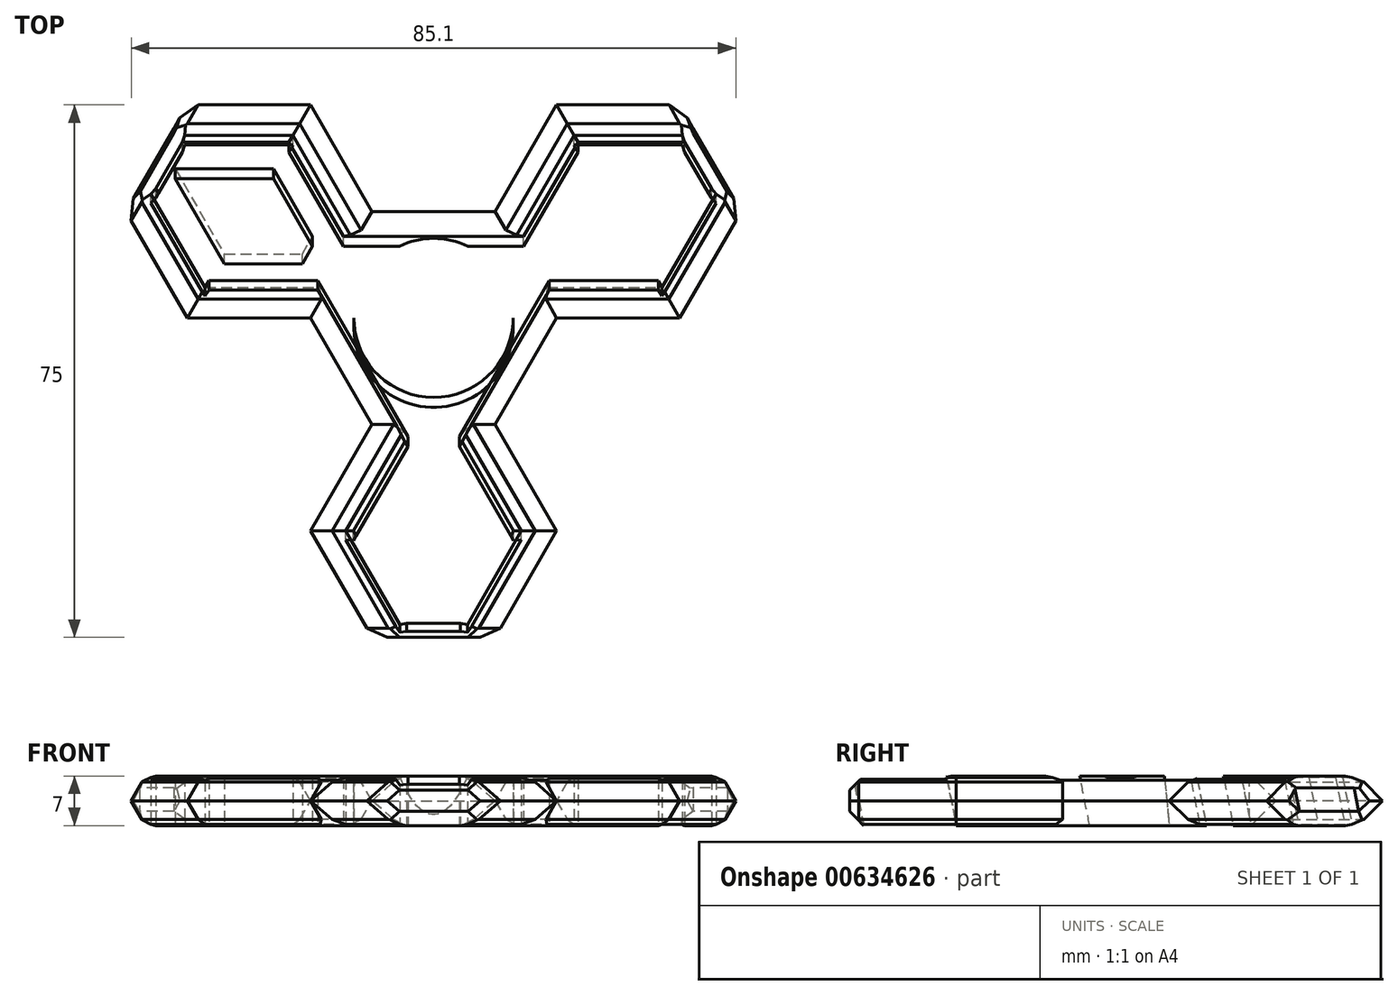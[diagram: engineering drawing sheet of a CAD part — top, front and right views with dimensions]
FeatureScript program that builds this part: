
annotation { "Feature Type Name" : "Feature", "Feature Type Description" : "" }
export const myFeature = defineFeature(function(context is Context, id is Id, definition is map)
    precondition{}
    {
        {
            var Q0;
            Q0=qCreatedBy(makeId("Top.planeOp"),FACE);
            var sketch = newSketch(context, id + "F0", { "sketchPlane" : qUnion([Q0])});
            skCircle(sketch, "E0", {"center": v(0, 0) * mm, "radius": 11.2 * mm});
            skCircle(sketch, "E1", {"center": v(0, 0) * mm, "radius": 15 * mm});
            skCircle(sketch, "E2.cCircle", {"center": v(0, 0) * mm, "radius": 15 * mm, "construction": true});
            skLineSegment(sketch, "E2.0", {"start": v(-8.66, 15) * mm, "end": v(8.66, 15) * mm});
            skLineSegment(sketch, "E2.1", {"start": v(8.66, 15) * mm, "end": v(17.32, 0) * mm});
            skLineSegment(sketch, "E2.2", {"start": v(17.32, 0) * mm, "end": v(8.66, -15) * mm});
            skLineSegment(sketch, "E2.3", {"start": v(8.66, -15) * mm, "end": v(-8.66, -15) * mm});
            skLineSegment(sketch, "E2.4", {"start": v(-8.66, -15) * mm, "end": v(-17.32, 0) * mm});
            skLineSegment(sketch, "E2.5", {"start": v(-17.32, 0) * mm, "end": v(-8.66, 15) * mm});
            skPoint(sketch, "E2.0.midPoint", {"position": v(0, 15) * mm});
            skLineSegment(sketch, "E3", {"start": v(-13, 7.5) * mm, "end": v(0, 0) * mm});
            skLineSegment(sketch, "E4", {"start": v(0, 0) * mm, "end": v(13, 7.5) * mm});
            skLineSegment(sketch, "E5", {"start": v(13, 7.5) * mm, "end": v(0, 0) * mm});
            skLineSegment(sketch, "E6", {"start": v(0, 0) * mm, "end": v(0, -15) * mm});
            skLineSegment(sketch, "E7", {"start": v(0, -15) * mm, "end": v(0, 0) * mm});
            skLineSegment(sketch, "E8", {"start": v(0, 0) * mm, "end": v(-34.64, 20) * mm});
            skLineSegment(sketch, "E9", {"start": v(-34.64, 20) * mm, "end": v(0, 0) * mm});
            skLineSegment(sketch, "E10", {"start": v(0, 0) * mm, "end": v(0, -40) * mm});
            skLineSegment(sketch, "E11", {"start": v(0, 0) * mm, "end": v(34.64, 20) * mm});
            skLineSegment(sketch, "E12", {"start": v(34.64, 20) * mm, "end": v(17.32, 10) * mm});
            skLineSegment(sketch, "E13", {"start": v(17.32, 10) * mm, "end": v(25.98, 15) * mm});
            skCircle(sketch, "E14.cCircle", {"center": v(25.98, 15) * mm, "radius": 15 * mm, "construction": true});
            skLineSegment(sketch, "E14.0", {"start": v(17.32, 0) * mm, "end": v(8.66, 15) * mm});
            skLineSegment(sketch, "E14.1", {"start": v(8.66, 15) * mm, "end": v(17.32, 30) * mm});
            skLineSegment(sketch, "E14.2", {"start": v(17.32, 30) * mm, "end": v(34.64, 30) * mm});
            skLineSegment(sketch, "E14.3", {"start": v(34.64, 30) * mm, "end": v(43.3, 15) * mm});
            skLineSegment(sketch, "E14.4", {"start": v(43.3, 15) * mm, "end": v(34.64, 0) * mm});
            skLineSegment(sketch, "E14.5", {"start": v(34.64, 0) * mm, "end": v(17.32, 0) * mm});
            skPoint(sketch, "E14.0.midPoint", {"position": v(13, 7.5) * mm});
            skCircle(sketch, "E15.cCircle", {"center": v(-25.98, 15) * mm, "radius": 15 * mm, "construction": true});
            skLineSegment(sketch, "E15.0", {"start": v(-8.66, 15) * mm, "end": v(-17.32, 0) * mm});
            skLineSegment(sketch, "E15.1", {"start": v(-17.32, 0) * mm, "end": v(-34.64, 0) * mm});
            skLineSegment(sketch, "E15.2", {"start": v(-34.64, 0) * mm, "end": v(-43.3, 15) * mm});
            skLineSegment(sketch, "E15.3", {"start": v(-43.3, 15) * mm, "end": v(-34.64, 30) * mm});
            skLineSegment(sketch, "E15.4", {"start": v(-34.64, 30) * mm, "end": v(-17.32, 30) * mm});
            skLineSegment(sketch, "E15.5", {"start": v(-17.32, 30) * mm, "end": v(-8.66, 15) * mm});
            skPoint(sketch, "E15.0.midPoint", {"position": v(-13, 7.5) * mm});
            skLineSegment(sketch, "E16", {"start": v(0, 0) * mm, "end": v(0, -20) * mm});
            skLineSegment(sketch, "E17", {"start": v(0, -20) * mm, "end": v(0, -30) * mm});
            skLineSegment(sketch, "E18", {"start": v(0, -20) * mm, "end": v(0, -40) * mm});
            skCircle(sketch, "E19.cCircle", {"center": v(0, -30) * mm, "radius": 15 * mm, "construction": true});
            skLineSegment(sketch, "E19.0", {"start": v(-8.66, -15) * mm, "end": v(8.66, -15) * mm});
            skLineSegment(sketch, "E19.1", {"start": v(8.66, -15) * mm, "end": v(17.32, -30) * mm});
            skLineSegment(sketch, "E19.2", {"start": v(17.32, -30) * mm, "end": v(8.66, -45) * mm});
            skLineSegment(sketch, "E19.3", {"start": v(8.66, -45) * mm, "end": v(-8.66, -45) * mm});
            skLineSegment(sketch, "E19.4", {"start": v(-8.66, -45) * mm, "end": v(-17.32, -30) * mm});
            skLineSegment(sketch, "E19.5", {"start": v(-17.32, -30) * mm, "end": v(-8.66, -15) * mm});
            skPoint(sketch, "E19.0.midPoint", {"position": v(0, -15) * mm});
            skSolve(sketch);
        }
        {
            var Q0;
            {var subQ0=sQuery(id+"F0.wireOp",EDGE,"E15.1");Q0=makeQuery(id+"F0.imprint","IMPRINT",FACE,{"disambiguationData":[TD([[makeQuery(id+"F0.imprint","IMPRINT",EDGE,{"derivedFrom":subQ0}),-1.0]])]});}
            var Q1;
            {var subQ0=sQuery(id+"F0.wireOp",EDGE,"E14.1");Q1=makeQuery(id+"F0.imprint","IMPRINT",FACE,{"disambiguationData":[TD([[makeQuery(id+"F0.imprint","IMPRINT",EDGE,{"derivedFrom":subQ0}),-1.0]])]});}
            var Q2;
            {var subQ0=sQuery(id+"F0.wireOp",EDGE,"E2.0");var subQ1=sQuery(id+"F0.wireOp",EDGE,"E1");var subQ2=makeQuery(id+"F0.imprint","INTERSECT",VERTEX,{"derivedFrom":[subQ1,subQ0]});Q2=makeQuery(id+"F0.imprint","IMPRINT",FACE,{"disambiguationData":[TD([[makeQuery(id+"F0.imprint","IMPRINT",EDGE,{"disambiguationData":[TD([[subQ2,1.0]])],"derivedFrom":subQ1}),-1.0]])]});}
            var Q3;
            {var subQ2=sQuery(id+"F0.wireOp",EDGE,"E9");var subQ4=sQuery(id+"F0.wireOp",EDGE,"E0");var subQ5=makeQuery(id+"F0.imprint","INTERSECT",VERTEX,{"derivedFrom":[subQ4,subQ2]});Q3=makeQuery(id+"F0.imprint","IMPRINT",FACE,{"disambiguationData":[TD([[makeQuery(id+"F0.imprint","IMPRINT",EDGE,{"disambiguationData":[TD([[subQ5,1.0]])],"derivedFrom":subQ4}),-1.0]])]});}
            var Q4;
            {var subQ0=sQuery(id+"F0.wireOp",EDGE,"E11");var subQ1=sQuery(id+"F0.wireOp",EDGE,"E0");var subQ2=makeQuery(id+"F0.imprint","INTERSECT",VERTEX,{"derivedFrom":[subQ1,subQ0]});Q4=makeQuery(id+"F0.imprint","IMPRINT",FACE,{"disambiguationData":[TD([[makeQuery(id+"F0.imprint","IMPRINT",EDGE,{"disambiguationData":[TD([[subQ2,1.0]])],"derivedFrom":subQ1}),-1.0]])]});}
            var Q5;
            {var subQ0=sQuery(id+"F0.wireOp",EDGE,"E2.2");var subQ1=sQuery(id+"F0.wireOp",EDGE,"E1");var subQ2=makeQuery(id+"F0.imprint","INTERSECT",VERTEX,{"derivedFrom":[subQ1,subQ0]});Q5=makeQuery(id+"F0.imprint","IMPRINT",FACE,{"disambiguationData":[TD([[makeQuery(id+"F0.imprint","IMPRINT",EDGE,{"disambiguationData":[TD([[subQ2,-1.0]])],"derivedFrom":subQ1}),-1.0]])]});}
            var Q6;
            {var subQ0=sQuery(id+"F0.wireOp",EDGE,"E19.1");Q6=makeQuery(id+"F0.imprint","IMPRINT",FACE,{"disambiguationData":[TD([[makeQuery(id+"F0.imprint","IMPRINT",EDGE,{"derivedFrom":subQ0}),-1.0]])]});}
            var Q7;
            {var subQ0=sQuery(id+"F0.wireOp",EDGE,"E2.2");var subQ1=sQuery(id+"F0.wireOp",EDGE,"E1");var subQ2=makeQuery(id+"F0.imprint","INTERSECT",VERTEX,{"derivedFrom":[subQ1,subQ0]});Q7=makeQuery(id+"F0.imprint","IMPRINT",FACE,{"disambiguationData":[TD([[makeQuery(id+"F0.imprint","IMPRINT",EDGE,{"disambiguationData":[TD([[subQ2,1.0]])],"derivedFrom":subQ1}),-1.0]])]});}
            var Q8;
            {var subQ0=sQuery(id+"F0.wireOp",EDGE,"E2.4");var subQ1=sQuery(id+"F0.wireOp",EDGE,"E1");var subQ2=makeQuery(id+"F0.imprint","INTERSECT",VERTEX,{"derivedFrom":[subQ1,subQ0]});Q8=makeQuery(id+"F0.imprint","IMPRINT",FACE,{"disambiguationData":[TD([[makeQuery(id+"F0.imprint","IMPRINT",EDGE,{"disambiguationData":[TD([[subQ2,-1.0]])],"derivedFrom":subQ1}),-1.0]])]});}
            var Q9;
            {var subQ0=sQuery(id+"F0.wireOp",EDGE,"E9");var subQ1=sQuery(id+"F0.wireOp",EDGE,"E0");var subQ2=makeQuery(id+"F0.imprint","INTERSECT",VERTEX,{"derivedFrom":[subQ1,subQ0]});Q9=makeQuery(id+"F0.imprint","IMPRINT",FACE,{"disambiguationData":[TD([[makeQuery(id+"F0.imprint","IMPRINT",EDGE,{"disambiguationData":[TD([[subQ2,-1.0]])],"derivedFrom":subQ1}),-1.0]])]});}
            var Q10;
            {var subQ0=sQuery(id+"F0.wireOp",EDGE,"E2.4");var subQ1=sQuery(id+"F0.wireOp",EDGE,"E1");var subQ2=makeQuery(id+"F0.imprint","INTERSECT",VERTEX,{"derivedFrom":[subQ1,subQ0]});Q10=makeQuery(id+"F0.imprint","IMPRINT",FACE,{"disambiguationData":[TD([[makeQuery(id+"F0.imprint","IMPRINT",EDGE,{"disambiguationData":[TD([[subQ2,1.0]])],"derivedFrom":subQ1}),-1.0]])]});}
            var Q11;
            {var subQ0=sQuery(id+"F0.wireOp",EDGE,"E2.0");var subQ1=sQuery(id+"F0.wireOp",EDGE,"E1");var subQ2=makeQuery(id+"F0.imprint","INTERSECT",VERTEX,{"derivedFrom":[subQ1,subQ0]});Q11=makeQuery(id+"F0.imprint","IMPRINT",FACE,{"disambiguationData":[TD([[makeQuery(id+"F0.imprint","IMPRINT",EDGE,{"disambiguationData":[TD([[subQ2,-1.0]])],"derivedFrom":subQ1}),-1.0]])]});}
            extrude(context, id + "F1", {"entities" : qUnion([Q0, Q1, Q2, Q3, Q4, Q5, Q6, Q7, Q8, Q9, Q10, Q11]), "depth" : 7 * mm, "offsetDistance" : 25 * mm});
        }
        {
            var Q0;
            Q0=makeQuery(id+"F1.opExtrude","CAP_EDGE",EDGE,{"disambiguationData":[OSD([sQuery(id+"F0.wireOp",EDGE,"E14.2")])],"isStart":true});
            var Q1;
            Q1=makeQuery(id+"F1.opExtrude","CAP_EDGE",EDGE,{"disambiguationData":[OSD([sQuery(id+"F0.wireOp",EDGE,"E14.1")])],"isStart":true});
            var Q2;
            Q2=makeQuery(id+"F1.opExtrude","CAP_EDGE",EDGE,{"disambiguationData":[OSD([sQuery(id+"F0.wireOp",EDGE,"E2.0")])],"isStart":true});
            var Q3;
            Q3=makeQuery(id+"F1.opExtrude","CAP_EDGE",EDGE,{"disambiguationData":[OSD([sQuery(id+"F0.wireOp",EDGE,"E15.5")])],"isStart":true});
            var Q4;
            Q4=makeQuery(id+"F1.opExtrude","CAP_EDGE",EDGE,{"disambiguationData":[OSD([sQuery(id+"F0.wireOp",EDGE,"E15.4")])],"isStart":true});
            var Q5;
            Q5=makeQuery(id+"F1.opExtrude","CAP_EDGE",EDGE,{"disambiguationData":[OSD([sQuery(id+"F0.wireOp",EDGE,"E15.2")])],"isStart":true});
            var Q6;
            Q6=makeQuery(id+"F1.opExtrude","CAP_EDGE",EDGE,{"disambiguationData":[OSD([sQuery(id+"F0.wireOp",EDGE,"E15.1")])],"isStart":true});
            var Q7;
            Q7=makeQuery(id+"F1.opExtrude","CAP_EDGE",EDGE,{"disambiguationData":[OSD([sQuery(id+"F0.wireOp",EDGE,"E2.4")])],"isStart":true});
            var Q8;
            Q8=makeQuery(id+"F1.opExtrude","CAP_EDGE",EDGE,{"disambiguationData":[OSD([sQuery(id+"F0.wireOp",EDGE,"E19.5")])],"isStart":true});
            var Q9;
            Q9=makeQuery(id+"F1.opExtrude","CAP_EDGE",EDGE,{"disambiguationData":[OSD([sQuery(id+"F0.wireOp",EDGE,"E19.4")])],"isStart":true});
            var Q10;
            Q10=makeQuery(id+"F1.opExtrude","CAP_EDGE",EDGE,{"disambiguationData":[OSD([sQuery(id+"F0.wireOp",EDGE,"E19.2")])],"isStart":true});
            var Q11;
            Q11=makeQuery(id+"F1.opExtrude","CAP_EDGE",EDGE,{"disambiguationData":[OSD([sQuery(id+"F0.wireOp",EDGE,"E19.1")])],"isStart":true});
            var Q12;
            Q12=makeQuery(id+"F1.opExtrude","CAP_EDGE",EDGE,{"disambiguationData":[OSD([sQuery(id+"F0.wireOp",EDGE,"E2.2")])],"isStart":true});
            var Q13;
            Q13=makeQuery(id+"F1.opExtrude","CAP_EDGE",EDGE,{"disambiguationData":[OSD([sQuery(id+"F0.wireOp",EDGE,"E14.5")])],"isStart":true});
            var Q14;
            Q14=makeQuery(id+"F1.opExtrude","CAP_EDGE",EDGE,{"disambiguationData":[OSD([sQuery(id+"F0.wireOp",EDGE,"E14.4")])],"isStart":true});
            var Q15;
            Q15=makeQuery(id+"F1.opExtrude","CAP_EDGE",EDGE,{"disambiguationData":[OSD([sQuery(id+"F0.wireOp",EDGE,"E15.4")])],"isStart":false});
            var Q16;
            Q16=makeQuery(id+"F1.opExtrude","CAP_EDGE",EDGE,{"disambiguationData":[OSD([sQuery(id+"F0.wireOp",EDGE,"E15.5")])],"isStart":false});
            var Q17;
            Q17=makeQuery(id+"F1.opExtrude","CAP_EDGE",EDGE,{"disambiguationData":[OSD([sQuery(id+"F0.wireOp",EDGE,"E2.0")])],"isStart":false});
            var Q18;
            Q18=makeQuery(id+"F1.opExtrude","CAP_EDGE",EDGE,{"disambiguationData":[OSD([sQuery(id+"F0.wireOp",EDGE,"E14.1")])],"isStart":false});
            var Q19;
            Q19=makeQuery(id+"F1.opExtrude","CAP_EDGE",EDGE,{"disambiguationData":[OSD([sQuery(id+"F0.wireOp",EDGE,"E14.2")])],"isStart":false});
            var Q20;
            Q20=makeQuery(id+"F1.opExtrude","CAP_EDGE",EDGE,{"disambiguationData":[OSD([sQuery(id+"F0.wireOp",EDGE,"E14.4")])],"isStart":false});
            var Q21;
            Q21=makeQuery(id+"F1.opExtrude","CAP_EDGE",EDGE,{"disambiguationData":[OSD([sQuery(id+"F0.wireOp",EDGE,"E2.2")])],"isStart":false});
            var Q22;
            Q22=makeQuery(id+"F1.opExtrude","CAP_EDGE",EDGE,{"disambiguationData":[OSD([sQuery(id+"F0.wireOp",EDGE,"E14.5")])],"isStart":false});
            var Q23;
            Q23=makeQuery(id+"F1.opExtrude","CAP_EDGE",EDGE,{"disambiguationData":[OSD([sQuery(id+"F0.wireOp",EDGE,"E19.1")])],"isStart":false});
            var Q24;
            Q24=makeQuery(id+"F1.opExtrude","CAP_EDGE",EDGE,{"disambiguationData":[OSD([sQuery(id+"F0.wireOp",EDGE,"E19.2")])],"isStart":false});
            var Q25;
            Q25=makeQuery(id+"F1.opExtrude","CAP_EDGE",EDGE,{"disambiguationData":[OSD([sQuery(id+"F0.wireOp",EDGE,"E19.4")])],"isStart":false});
            var Q26;
            Q26=makeQuery(id+"F1.opExtrude","CAP_EDGE",EDGE,{"disambiguationData":[OSD([sQuery(id+"F0.wireOp",EDGE,"E19.5")])],"isStart":false});
            var Q27;
            Q27=makeQuery(id+"F1.opExtrude","CAP_EDGE",EDGE,{"disambiguationData":[OSD([sQuery(id+"F0.wireOp",EDGE,"E2.4")])],"isStart":false});
            var Q28;
            Q28=makeQuery(id+"F1.opExtrude","CAP_EDGE",EDGE,{"disambiguationData":[OSD([sQuery(id+"F0.wireOp",EDGE,"E15.2")])],"isStart":false});
            chamfer(context, id + "F2", {"entities" : qUnion([Q0, Q1, Q2, Q3, Q4, Q5, Q6, Q7, Q8, Q9, Q10, Q11, Q12, Q13, Q14, Q15, Q16, Q17, Q18, Q19, Q20, Q21, Q22, Q23, Q24, Q25, Q26, Q27, Q28]), "width" : 3.5 * mm, "tangentPropagation" : true});
        }
        {
            var Q0;
            Q0=makeQuery(id+"F1.opExtrude","CAP_EDGE",EDGE,{"disambiguationData":[OSD([sQuery(id+"F0.wireOp",EDGE,"E15.1")])],"isStart":false});
            chamfer(context, id + "F3", {"entities" : qUnion([Q0]), "width" : 3.5 * mm, "tangentPropagation" : true});
        }
        {
            var Q0;
            Q0=makeQuery(id+"F1.opExtrude","SWEPT_FACE",FACE,{"disambiguationData":[OSD([sQuery(id+"F0.wireOp",EDGE,"E14.3")])]});
            var Q1;
            Q1=makeQuery(id+"F1.opExtrude","SWEPT_FACE",FACE,{"disambiguationData":[OSD([sQuery(id+"F0.wireOp",EDGE,"E15.3")])]});
            var Q2;
            Q2=makeQuery(id+"F1.opExtrude","SWEPT_FACE",FACE,{"disambiguationData":[OSD([sQuery(id+"F0.wireOp",EDGE,"E19.3")])]});
            chamfer(context, id + "F4", {"entities" : qUnion([Q0, Q1, Q2]), "width" : 2 * mm, "tangentPropagation" : true});
        }
        {
            var Q0;
            {var subQ0=sQuery(id+"F0.wireOp",EDGE,"E19.5");Q0=makeQuery(id+"F2.opChamfer","BLEND_EDGE",EDGE,{"blendedFrom":[makeQuery(id+"F1.opExtrude","CAP_EDGE",EDGE,{"disambiguationData":[OSD([subQ0])],"isStart":false}),makeQuery(id+"F1.opExtrude","CAP_FACE",FACE,{"disambiguationData":[OSD([sQuery(id+"F0.wireOp",EDGE,"E0"),sQuery(id+"F0.wireOp",EDGE,"E2.0"),sQuery(id+"F0.wireOp",EDGE,"E2.2"),sQuery(id+"F0.wireOp",EDGE,"E2.4"),sQuery(id+"F0.wireOp",EDGE,"E14.1"),sQuery(id+"F0.wireOp",EDGE,"E14.2"),sQuery(id+"F0.wireOp",EDGE,"E14.3"),sQuery(id+"F0.wireOp",EDGE,"E14.4"),sQuery(id+"F0.wireOp",EDGE,"E14.5"),sQuery(id+"F0.wireOp",EDGE,"E15.1"),sQuery(id+"F0.wireOp",EDGE,"E15.2"),sQuery(id+"F0.wireOp",EDGE,"E15.3"),sQuery(id+"F0.wireOp",EDGE,"E15.4"),sQuery(id+"F0.wireOp",EDGE,"E15.5"),sQuery(id+"F0.wireOp",EDGE,"E19.1"),sQuery(id+"F0.wireOp",EDGE,"E19.2"),sQuery(id+"F0.wireOp",EDGE,"E19.3"),sQuery(id+"F0.wireOp",EDGE,"E19.4"),subQ0])],"isStart":false})],"blendedInto":[makeQuery(id+"F1.opExtrude","CAP_FACE",FACE,{"disambiguationData":[OSD([sQuery(id+"F0.wireOp",EDGE,"E0"),sQuery(id+"F0.wireOp",EDGE,"E2.0"),sQuery(id+"F0.wireOp",EDGE,"E2.2"),sQuery(id+"F0.wireOp",EDGE,"E2.4"),sQuery(id+"F0.wireOp",EDGE,"E14.1"),sQuery(id+"F0.wireOp",EDGE,"E14.2"),sQuery(id+"F0.wireOp",EDGE,"E14.3"),sQuery(id+"F0.wireOp",EDGE,"E14.4"),sQuery(id+"F0.wireOp",EDGE,"E14.5"),sQuery(id+"F0.wireOp",EDGE,"E15.1"),sQuery(id+"F0.wireOp",EDGE,"E15.2"),sQuery(id+"F0.wireOp",EDGE,"E15.3"),sQuery(id+"F0.wireOp",EDGE,"E15.4"),sQuery(id+"F0.wireOp",EDGE,"E15.5"),sQuery(id+"F0.wireOp",EDGE,"E19.1"),sQuery(id+"F0.wireOp",EDGE,"E19.2"),sQuery(id+"F0.wireOp",EDGE,"E19.3"),sQuery(id+"F0.wireOp",EDGE,"E19.4"),subQ0])],"isStart":false})]});}
            var Q1;
            {var subQ0=sQuery(id+"F0.wireOp",EDGE,"E19.4");Q1=makeQuery(id+"F2.opChamfer","BLEND_EDGE",EDGE,{"blendedFrom":[makeQuery(id+"F1.opExtrude","CAP_EDGE",EDGE,{"disambiguationData":[OSD([subQ0])],"isStart":false}),makeQuery(id+"F1.opExtrude","CAP_FACE",FACE,{"disambiguationData":[OSD([sQuery(id+"F0.wireOp",EDGE,"E0"),sQuery(id+"F0.wireOp",EDGE,"E2.0"),sQuery(id+"F0.wireOp",EDGE,"E2.2"),sQuery(id+"F0.wireOp",EDGE,"E2.4"),sQuery(id+"F0.wireOp",EDGE,"E14.1"),sQuery(id+"F0.wireOp",EDGE,"E14.2"),sQuery(id+"F0.wireOp",EDGE,"E14.3"),sQuery(id+"F0.wireOp",EDGE,"E14.4"),sQuery(id+"F0.wireOp",EDGE,"E14.5"),sQuery(id+"F0.wireOp",EDGE,"E15.1"),sQuery(id+"F0.wireOp",EDGE,"E15.2"),sQuery(id+"F0.wireOp",EDGE,"E15.3"),sQuery(id+"F0.wireOp",EDGE,"E15.4"),sQuery(id+"F0.wireOp",EDGE,"E15.5"),sQuery(id+"F0.wireOp",EDGE,"E19.1"),sQuery(id+"F0.wireOp",EDGE,"E19.2"),sQuery(id+"F0.wireOp",EDGE,"E19.3"),subQ0,sQuery(id+"F0.wireOp",EDGE,"E19.5")])],"isStart":false})],"blendedInto":[makeQuery(id+"F1.opExtrude","CAP_FACE",FACE,{"disambiguationData":[OSD([sQuery(id+"F0.wireOp",EDGE,"E0"),sQuery(id+"F0.wireOp",EDGE,"E2.0"),sQuery(id+"F0.wireOp",EDGE,"E2.2"),sQuery(id+"F0.wireOp",EDGE,"E2.4"),sQuery(id+"F0.wireOp",EDGE,"E14.1"),sQuery(id+"F0.wireOp",EDGE,"E14.2"),sQuery(id+"F0.wireOp",EDGE,"E14.3"),sQuery(id+"F0.wireOp",EDGE,"E14.4"),sQuery(id+"F0.wireOp",EDGE,"E14.5"),sQuery(id+"F0.wireOp",EDGE,"E15.1"),sQuery(id+"F0.wireOp",EDGE,"E15.2"),sQuery(id+"F0.wireOp",EDGE,"E15.3"),sQuery(id+"F0.wireOp",EDGE,"E15.4"),sQuery(id+"F0.wireOp",EDGE,"E15.5"),sQuery(id+"F0.wireOp",EDGE,"E19.1"),sQuery(id+"F0.wireOp",EDGE,"E19.2"),sQuery(id+"F0.wireOp",EDGE,"E19.3"),subQ0,sQuery(id+"F0.wireOp",EDGE,"E19.5")])],"isStart":false})]});}
            var Q2;
            {var subQ0=sQuery(id+"F0.wireOp",EDGE,"E19.2");Q2=makeQuery(id+"F2.opChamfer","BLEND_EDGE",EDGE,{"blendedFrom":[makeQuery(id+"F1.opExtrude","CAP_EDGE",EDGE,{"disambiguationData":[OSD([subQ0])],"isStart":false}),makeQuery(id+"F1.opExtrude","CAP_FACE",FACE,{"disambiguationData":[OSD([sQuery(id+"F0.wireOp",EDGE,"E0"),sQuery(id+"F0.wireOp",EDGE,"E2.0"),sQuery(id+"F0.wireOp",EDGE,"E2.2"),sQuery(id+"F0.wireOp",EDGE,"E2.4"),sQuery(id+"F0.wireOp",EDGE,"E14.1"),sQuery(id+"F0.wireOp",EDGE,"E14.2"),sQuery(id+"F0.wireOp",EDGE,"E14.3"),sQuery(id+"F0.wireOp",EDGE,"E14.4"),sQuery(id+"F0.wireOp",EDGE,"E14.5"),sQuery(id+"F0.wireOp",EDGE,"E15.1"),sQuery(id+"F0.wireOp",EDGE,"E15.2"),sQuery(id+"F0.wireOp",EDGE,"E15.3"),sQuery(id+"F0.wireOp",EDGE,"E15.4"),sQuery(id+"F0.wireOp",EDGE,"E15.5"),sQuery(id+"F0.wireOp",EDGE,"E19.1"),subQ0,sQuery(id+"F0.wireOp",EDGE,"E19.3"),sQuery(id+"F0.wireOp",EDGE,"E19.4"),sQuery(id+"F0.wireOp",EDGE,"E19.5")])],"isStart":false})],"blendedInto":[makeQuery(id+"F1.opExtrude","CAP_FACE",FACE,{"disambiguationData":[OSD([sQuery(id+"F0.wireOp",EDGE,"E0"),sQuery(id+"F0.wireOp",EDGE,"E2.0"),sQuery(id+"F0.wireOp",EDGE,"E2.2"),sQuery(id+"F0.wireOp",EDGE,"E2.4"),sQuery(id+"F0.wireOp",EDGE,"E14.1"),sQuery(id+"F0.wireOp",EDGE,"E14.2"),sQuery(id+"F0.wireOp",EDGE,"E14.3"),sQuery(id+"F0.wireOp",EDGE,"E14.4"),sQuery(id+"F0.wireOp",EDGE,"E14.5"),sQuery(id+"F0.wireOp",EDGE,"E15.1"),sQuery(id+"F0.wireOp",EDGE,"E15.2"),sQuery(id+"F0.wireOp",EDGE,"E15.3"),sQuery(id+"F0.wireOp",EDGE,"E15.4"),sQuery(id+"F0.wireOp",EDGE,"E15.5"),sQuery(id+"F0.wireOp",EDGE,"E19.1"),subQ0,sQuery(id+"F0.wireOp",EDGE,"E19.3"),sQuery(id+"F0.wireOp",EDGE,"E19.4"),sQuery(id+"F0.wireOp",EDGE,"E19.5")])],"isStart":false})]});}
            var Q3;
            {var subQ0=sQuery(id+"F0.wireOp",EDGE,"E19.1");Q3=makeQuery(id+"F2.opChamfer","BLEND_EDGE",EDGE,{"blendedFrom":[makeQuery(id+"F1.opExtrude","CAP_EDGE",EDGE,{"disambiguationData":[OSD([subQ0])],"isStart":false}),makeQuery(id+"F1.opExtrude","CAP_FACE",FACE,{"disambiguationData":[OSD([sQuery(id+"F0.wireOp",EDGE,"E0"),sQuery(id+"F0.wireOp",EDGE,"E2.0"),sQuery(id+"F0.wireOp",EDGE,"E2.2"),sQuery(id+"F0.wireOp",EDGE,"E2.4"),sQuery(id+"F0.wireOp",EDGE,"E14.1"),sQuery(id+"F0.wireOp",EDGE,"E14.2"),sQuery(id+"F0.wireOp",EDGE,"E14.3"),sQuery(id+"F0.wireOp",EDGE,"E14.4"),sQuery(id+"F0.wireOp",EDGE,"E14.5"),sQuery(id+"F0.wireOp",EDGE,"E15.1"),sQuery(id+"F0.wireOp",EDGE,"E15.2"),sQuery(id+"F0.wireOp",EDGE,"E15.3"),sQuery(id+"F0.wireOp",EDGE,"E15.4"),sQuery(id+"F0.wireOp",EDGE,"E15.5"),subQ0,sQuery(id+"F0.wireOp",EDGE,"E19.2"),sQuery(id+"F0.wireOp",EDGE,"E19.3"),sQuery(id+"F0.wireOp",EDGE,"E19.4"),sQuery(id+"F0.wireOp",EDGE,"E19.5")])],"isStart":false})],"blendedInto":[makeQuery(id+"F1.opExtrude","CAP_FACE",FACE,{"disambiguationData":[OSD([sQuery(id+"F0.wireOp",EDGE,"E0"),sQuery(id+"F0.wireOp",EDGE,"E2.0"),sQuery(id+"F0.wireOp",EDGE,"E2.2"),sQuery(id+"F0.wireOp",EDGE,"E2.4"),sQuery(id+"F0.wireOp",EDGE,"E14.1"),sQuery(id+"F0.wireOp",EDGE,"E14.2"),sQuery(id+"F0.wireOp",EDGE,"E14.3"),sQuery(id+"F0.wireOp",EDGE,"E14.4"),sQuery(id+"F0.wireOp",EDGE,"E14.5"),sQuery(id+"F0.wireOp",EDGE,"E15.1"),sQuery(id+"F0.wireOp",EDGE,"E15.2"),sQuery(id+"F0.wireOp",EDGE,"E15.3"),sQuery(id+"F0.wireOp",EDGE,"E15.4"),sQuery(id+"F0.wireOp",EDGE,"E15.5"),subQ0,sQuery(id+"F0.wireOp",EDGE,"E19.2"),sQuery(id+"F0.wireOp",EDGE,"E19.3"),sQuery(id+"F0.wireOp",EDGE,"E19.4"),sQuery(id+"F0.wireOp",EDGE,"E19.5")])],"isStart":false})]});}
            var Q4;
            {var subQ0=sQuery(id+"F0.wireOp",EDGE,"E15.1");Q4=makeQuery(id+"F3.opChamfer","BLEND_EDGE",EDGE,{"blendedFrom":[makeQuery(id+"F1.opExtrude","CAP_EDGE",EDGE,{"disambiguationData":[OSD([subQ0])],"isStart":false}),makeQuery(id+"F1.opExtrude","CAP_FACE",FACE,{"disambiguationData":[OSD([sQuery(id+"F0.wireOp",EDGE,"E0"),sQuery(id+"F0.wireOp",EDGE,"E2.0"),sQuery(id+"F0.wireOp",EDGE,"E2.2"),sQuery(id+"F0.wireOp",EDGE,"E2.4"),sQuery(id+"F0.wireOp",EDGE,"E14.1"),sQuery(id+"F0.wireOp",EDGE,"E14.2"),sQuery(id+"F0.wireOp",EDGE,"E14.3"),sQuery(id+"F0.wireOp",EDGE,"E14.4"),sQuery(id+"F0.wireOp",EDGE,"E14.5"),subQ0,sQuery(id+"F0.wireOp",EDGE,"E15.2"),sQuery(id+"F0.wireOp",EDGE,"E15.3"),sQuery(id+"F0.wireOp",EDGE,"E15.4"),sQuery(id+"F0.wireOp",EDGE,"E15.5"),sQuery(id+"F0.wireOp",EDGE,"E19.1"),sQuery(id+"F0.wireOp",EDGE,"E19.2"),sQuery(id+"F0.wireOp",EDGE,"E19.3"),sQuery(id+"F0.wireOp",EDGE,"E19.4"),sQuery(id+"F0.wireOp",EDGE,"E19.5")])],"isStart":false})],"blendedInto":[makeQuery(id+"F1.opExtrude","CAP_FACE",FACE,{"disambiguationData":[OSD([sQuery(id+"F0.wireOp",EDGE,"E0"),sQuery(id+"F0.wireOp",EDGE,"E2.0"),sQuery(id+"F0.wireOp",EDGE,"E2.2"),sQuery(id+"F0.wireOp",EDGE,"E2.4"),sQuery(id+"F0.wireOp",EDGE,"E14.1"),sQuery(id+"F0.wireOp",EDGE,"E14.2"),sQuery(id+"F0.wireOp",EDGE,"E14.3"),sQuery(id+"F0.wireOp",EDGE,"E14.4"),sQuery(id+"F0.wireOp",EDGE,"E14.5"),subQ0,sQuery(id+"F0.wireOp",EDGE,"E15.2"),sQuery(id+"F0.wireOp",EDGE,"E15.3"),sQuery(id+"F0.wireOp",EDGE,"E15.4"),sQuery(id+"F0.wireOp",EDGE,"E15.5"),sQuery(id+"F0.wireOp",EDGE,"E19.1"),sQuery(id+"F0.wireOp",EDGE,"E19.2"),sQuery(id+"F0.wireOp",EDGE,"E19.3"),sQuery(id+"F0.wireOp",EDGE,"E19.4"),sQuery(id+"F0.wireOp",EDGE,"E19.5")])],"isStart":false})]});}
            var Q5;
            {var subQ0=sQuery(id+"F0.wireOp",EDGE,"E15.2");Q5=makeQuery(id+"F2.opChamfer","BLEND_EDGE",EDGE,{"blendedFrom":[makeQuery(id+"F1.opExtrude","CAP_EDGE",EDGE,{"disambiguationData":[OSD([subQ0])],"isStart":false}),makeQuery(id+"F1.opExtrude","CAP_FACE",FACE,{"disambiguationData":[OSD([sQuery(id+"F0.wireOp",EDGE,"E0"),sQuery(id+"F0.wireOp",EDGE,"E2.0"),sQuery(id+"F0.wireOp",EDGE,"E2.2"),sQuery(id+"F0.wireOp",EDGE,"E2.4"),sQuery(id+"F0.wireOp",EDGE,"E14.1"),sQuery(id+"F0.wireOp",EDGE,"E14.2"),sQuery(id+"F0.wireOp",EDGE,"E14.3"),sQuery(id+"F0.wireOp",EDGE,"E14.4"),sQuery(id+"F0.wireOp",EDGE,"E14.5"),sQuery(id+"F0.wireOp",EDGE,"E15.1"),subQ0,sQuery(id+"F0.wireOp",EDGE,"E15.3"),sQuery(id+"F0.wireOp",EDGE,"E15.4"),sQuery(id+"F0.wireOp",EDGE,"E15.5"),sQuery(id+"F0.wireOp",EDGE,"E19.1"),sQuery(id+"F0.wireOp",EDGE,"E19.2"),sQuery(id+"F0.wireOp",EDGE,"E19.3"),sQuery(id+"F0.wireOp",EDGE,"E19.4"),sQuery(id+"F0.wireOp",EDGE,"E19.5")])],"isStart":false})],"blendedInto":[makeQuery(id+"F1.opExtrude","CAP_FACE",FACE,{"disambiguationData":[OSD([sQuery(id+"F0.wireOp",EDGE,"E0"),sQuery(id+"F0.wireOp",EDGE,"E2.0"),sQuery(id+"F0.wireOp",EDGE,"E2.2"),sQuery(id+"F0.wireOp",EDGE,"E2.4"),sQuery(id+"F0.wireOp",EDGE,"E14.1"),sQuery(id+"F0.wireOp",EDGE,"E14.2"),sQuery(id+"F0.wireOp",EDGE,"E14.3"),sQuery(id+"F0.wireOp",EDGE,"E14.4"),sQuery(id+"F0.wireOp",EDGE,"E14.5"),sQuery(id+"F0.wireOp",EDGE,"E15.1"),subQ0,sQuery(id+"F0.wireOp",EDGE,"E15.3"),sQuery(id+"F0.wireOp",EDGE,"E15.4"),sQuery(id+"F0.wireOp",EDGE,"E15.5"),sQuery(id+"F0.wireOp",EDGE,"E19.1"),sQuery(id+"F0.wireOp",EDGE,"E19.2"),sQuery(id+"F0.wireOp",EDGE,"E19.3"),sQuery(id+"F0.wireOp",EDGE,"E19.4"),sQuery(id+"F0.wireOp",EDGE,"E19.5")])],"isStart":false})]});}
            var Q6;
            {var subQ0=sQuery(id+"F0.wireOp",EDGE,"E15.4");Q6=makeQuery(id+"F2.opChamfer","BLEND_EDGE",EDGE,{"blendedFrom":[makeQuery(id+"F1.opExtrude","CAP_EDGE",EDGE,{"disambiguationData":[OSD([subQ0])],"isStart":false}),makeQuery(id+"F1.opExtrude","CAP_FACE",FACE,{"disambiguationData":[OSD([sQuery(id+"F0.wireOp",EDGE,"E0"),sQuery(id+"F0.wireOp",EDGE,"E2.0"),sQuery(id+"F0.wireOp",EDGE,"E2.2"),sQuery(id+"F0.wireOp",EDGE,"E2.4"),sQuery(id+"F0.wireOp",EDGE,"E14.1"),sQuery(id+"F0.wireOp",EDGE,"E14.2"),sQuery(id+"F0.wireOp",EDGE,"E14.3"),sQuery(id+"F0.wireOp",EDGE,"E14.4"),sQuery(id+"F0.wireOp",EDGE,"E14.5"),sQuery(id+"F0.wireOp",EDGE,"E15.1"),sQuery(id+"F0.wireOp",EDGE,"E15.2"),sQuery(id+"F0.wireOp",EDGE,"E15.3"),subQ0,sQuery(id+"F0.wireOp",EDGE,"E15.5"),sQuery(id+"F0.wireOp",EDGE,"E19.1"),sQuery(id+"F0.wireOp",EDGE,"E19.2"),sQuery(id+"F0.wireOp",EDGE,"E19.3"),sQuery(id+"F0.wireOp",EDGE,"E19.4"),sQuery(id+"F0.wireOp",EDGE,"E19.5")])],"isStart":false})],"blendedInto":[makeQuery(id+"F1.opExtrude","CAP_FACE",FACE,{"disambiguationData":[OSD([sQuery(id+"F0.wireOp",EDGE,"E0"),sQuery(id+"F0.wireOp",EDGE,"E2.0"),sQuery(id+"F0.wireOp",EDGE,"E2.2"),sQuery(id+"F0.wireOp",EDGE,"E2.4"),sQuery(id+"F0.wireOp",EDGE,"E14.1"),sQuery(id+"F0.wireOp",EDGE,"E14.2"),sQuery(id+"F0.wireOp",EDGE,"E14.3"),sQuery(id+"F0.wireOp",EDGE,"E14.4"),sQuery(id+"F0.wireOp",EDGE,"E14.5"),sQuery(id+"F0.wireOp",EDGE,"E15.1"),sQuery(id+"F0.wireOp",EDGE,"E15.2"),sQuery(id+"F0.wireOp",EDGE,"E15.3"),subQ0,sQuery(id+"F0.wireOp",EDGE,"E15.5"),sQuery(id+"F0.wireOp",EDGE,"E19.1"),sQuery(id+"F0.wireOp",EDGE,"E19.2"),sQuery(id+"F0.wireOp",EDGE,"E19.3"),sQuery(id+"F0.wireOp",EDGE,"E19.4"),sQuery(id+"F0.wireOp",EDGE,"E19.5")])],"isStart":false})]});}
            var Q7;
            {var subQ0=sQuery(id+"F0.wireOp",EDGE,"E15.5");Q7=makeQuery(id+"F2.opChamfer","BLEND_EDGE",EDGE,{"blendedFrom":[makeQuery(id+"F1.opExtrude","CAP_EDGE",EDGE,{"disambiguationData":[OSD([subQ0])],"isStart":false}),makeQuery(id+"F1.opExtrude","CAP_FACE",FACE,{"disambiguationData":[OSD([sQuery(id+"F0.wireOp",EDGE,"E0"),sQuery(id+"F0.wireOp",EDGE,"E2.0"),sQuery(id+"F0.wireOp",EDGE,"E2.2"),sQuery(id+"F0.wireOp",EDGE,"E2.4"),sQuery(id+"F0.wireOp",EDGE,"E14.1"),sQuery(id+"F0.wireOp",EDGE,"E14.2"),sQuery(id+"F0.wireOp",EDGE,"E14.3"),sQuery(id+"F0.wireOp",EDGE,"E14.4"),sQuery(id+"F0.wireOp",EDGE,"E14.5"),sQuery(id+"F0.wireOp",EDGE,"E15.1"),sQuery(id+"F0.wireOp",EDGE,"E15.2"),sQuery(id+"F0.wireOp",EDGE,"E15.3"),sQuery(id+"F0.wireOp",EDGE,"E15.4"),subQ0,sQuery(id+"F0.wireOp",EDGE,"E19.1"),sQuery(id+"F0.wireOp",EDGE,"E19.2"),sQuery(id+"F0.wireOp",EDGE,"E19.3"),sQuery(id+"F0.wireOp",EDGE,"E19.4"),sQuery(id+"F0.wireOp",EDGE,"E19.5")])],"isStart":false})],"blendedInto":[makeQuery(id+"F1.opExtrude","CAP_FACE",FACE,{"disambiguationData":[OSD([sQuery(id+"F0.wireOp",EDGE,"E0"),sQuery(id+"F0.wireOp",EDGE,"E2.0"),sQuery(id+"F0.wireOp",EDGE,"E2.2"),sQuery(id+"F0.wireOp",EDGE,"E2.4"),sQuery(id+"F0.wireOp",EDGE,"E14.1"),sQuery(id+"F0.wireOp",EDGE,"E14.2"),sQuery(id+"F0.wireOp",EDGE,"E14.3"),sQuery(id+"F0.wireOp",EDGE,"E14.4"),sQuery(id+"F0.wireOp",EDGE,"E14.5"),sQuery(id+"F0.wireOp",EDGE,"E15.1"),sQuery(id+"F0.wireOp",EDGE,"E15.2"),sQuery(id+"F0.wireOp",EDGE,"E15.3"),sQuery(id+"F0.wireOp",EDGE,"E15.4"),subQ0,sQuery(id+"F0.wireOp",EDGE,"E19.1"),sQuery(id+"F0.wireOp",EDGE,"E19.2"),sQuery(id+"F0.wireOp",EDGE,"E19.3"),sQuery(id+"F0.wireOp",EDGE,"E19.4"),sQuery(id+"F0.wireOp",EDGE,"E19.5")])],"isStart":false})]});}
            var Q8;
            {var subQ0=sQuery(id+"F0.wireOp",EDGE,"E14.5");Q8=makeQuery(id+"F2.opChamfer","BLEND_EDGE",EDGE,{"blendedFrom":[makeQuery(id+"F1.opExtrude","CAP_EDGE",EDGE,{"disambiguationData":[OSD([subQ0])],"isStart":false}),makeQuery(id+"F1.opExtrude","CAP_FACE",FACE,{"disambiguationData":[OSD([sQuery(id+"F0.wireOp",EDGE,"E0"),sQuery(id+"F0.wireOp",EDGE,"E2.0"),sQuery(id+"F0.wireOp",EDGE,"E2.2"),sQuery(id+"F0.wireOp",EDGE,"E2.4"),sQuery(id+"F0.wireOp",EDGE,"E14.1"),sQuery(id+"F0.wireOp",EDGE,"E14.2"),sQuery(id+"F0.wireOp",EDGE,"E14.3"),sQuery(id+"F0.wireOp",EDGE,"E14.4"),subQ0,sQuery(id+"F0.wireOp",EDGE,"E15.1"),sQuery(id+"F0.wireOp",EDGE,"E15.2"),sQuery(id+"F0.wireOp",EDGE,"E15.3"),sQuery(id+"F0.wireOp",EDGE,"E15.4"),sQuery(id+"F0.wireOp",EDGE,"E15.5"),sQuery(id+"F0.wireOp",EDGE,"E19.1"),sQuery(id+"F0.wireOp",EDGE,"E19.2"),sQuery(id+"F0.wireOp",EDGE,"E19.3"),sQuery(id+"F0.wireOp",EDGE,"E19.4"),sQuery(id+"F0.wireOp",EDGE,"E19.5")])],"isStart":false})],"blendedInto":[makeQuery(id+"F1.opExtrude","CAP_FACE",FACE,{"disambiguationData":[OSD([sQuery(id+"F0.wireOp",EDGE,"E0"),sQuery(id+"F0.wireOp",EDGE,"E2.0"),sQuery(id+"F0.wireOp",EDGE,"E2.2"),sQuery(id+"F0.wireOp",EDGE,"E2.4"),sQuery(id+"F0.wireOp",EDGE,"E14.1"),sQuery(id+"F0.wireOp",EDGE,"E14.2"),sQuery(id+"F0.wireOp",EDGE,"E14.3"),sQuery(id+"F0.wireOp",EDGE,"E14.4"),subQ0,sQuery(id+"F0.wireOp",EDGE,"E15.1"),sQuery(id+"F0.wireOp",EDGE,"E15.2"),sQuery(id+"F0.wireOp",EDGE,"E15.3"),sQuery(id+"F0.wireOp",EDGE,"E15.4"),sQuery(id+"F0.wireOp",EDGE,"E15.5"),sQuery(id+"F0.wireOp",EDGE,"E19.1"),sQuery(id+"F0.wireOp",EDGE,"E19.2"),sQuery(id+"F0.wireOp",EDGE,"E19.3"),sQuery(id+"F0.wireOp",EDGE,"E19.4"),sQuery(id+"F0.wireOp",EDGE,"E19.5")])],"isStart":false})]});}
            var Q9;
            {var subQ0=sQuery(id+"F0.wireOp",EDGE,"E14.4");Q9=makeQuery(id+"F2.opChamfer","BLEND_EDGE",EDGE,{"blendedFrom":[makeQuery(id+"F1.opExtrude","CAP_EDGE",EDGE,{"disambiguationData":[OSD([subQ0])],"isStart":false}),makeQuery(id+"F1.opExtrude","CAP_FACE",FACE,{"disambiguationData":[OSD([sQuery(id+"F0.wireOp",EDGE,"E0"),sQuery(id+"F0.wireOp",EDGE,"E2.0"),sQuery(id+"F0.wireOp",EDGE,"E2.2"),sQuery(id+"F0.wireOp",EDGE,"E2.4"),sQuery(id+"F0.wireOp",EDGE,"E14.1"),sQuery(id+"F0.wireOp",EDGE,"E14.2"),sQuery(id+"F0.wireOp",EDGE,"E14.3"),subQ0,sQuery(id+"F0.wireOp",EDGE,"E14.5"),sQuery(id+"F0.wireOp",EDGE,"E15.1"),sQuery(id+"F0.wireOp",EDGE,"E15.2"),sQuery(id+"F0.wireOp",EDGE,"E15.3"),sQuery(id+"F0.wireOp",EDGE,"E15.4"),sQuery(id+"F0.wireOp",EDGE,"E15.5"),sQuery(id+"F0.wireOp",EDGE,"E19.1"),sQuery(id+"F0.wireOp",EDGE,"E19.2"),sQuery(id+"F0.wireOp",EDGE,"E19.3"),sQuery(id+"F0.wireOp",EDGE,"E19.4"),sQuery(id+"F0.wireOp",EDGE,"E19.5")])],"isStart":false})],"blendedInto":[makeQuery(id+"F1.opExtrude","CAP_FACE",FACE,{"disambiguationData":[OSD([sQuery(id+"F0.wireOp",EDGE,"E0"),sQuery(id+"F0.wireOp",EDGE,"E2.0"),sQuery(id+"F0.wireOp",EDGE,"E2.2"),sQuery(id+"F0.wireOp",EDGE,"E2.4"),sQuery(id+"F0.wireOp",EDGE,"E14.1"),sQuery(id+"F0.wireOp",EDGE,"E14.2"),sQuery(id+"F0.wireOp",EDGE,"E14.3"),subQ0,sQuery(id+"F0.wireOp",EDGE,"E14.5"),sQuery(id+"F0.wireOp",EDGE,"E15.1"),sQuery(id+"F0.wireOp",EDGE,"E15.2"),sQuery(id+"F0.wireOp",EDGE,"E15.3"),sQuery(id+"F0.wireOp",EDGE,"E15.4"),sQuery(id+"F0.wireOp",EDGE,"E15.5"),sQuery(id+"F0.wireOp",EDGE,"E19.1"),sQuery(id+"F0.wireOp",EDGE,"E19.2"),sQuery(id+"F0.wireOp",EDGE,"E19.3"),sQuery(id+"F0.wireOp",EDGE,"E19.4"),sQuery(id+"F0.wireOp",EDGE,"E19.5")])],"isStart":false})]});}
            var Q10;
            {var subQ0=sQuery(id+"F0.wireOp",EDGE,"E14.1");Q10=makeQuery(id+"F2.opChamfer","BLEND_EDGE",EDGE,{"blendedFrom":[makeQuery(id+"F1.opExtrude","CAP_EDGE",EDGE,{"disambiguationData":[OSD([subQ0])],"isStart":false}),makeQuery(id+"F1.opExtrude","CAP_FACE",FACE,{"disambiguationData":[OSD([sQuery(id+"F0.wireOp",EDGE,"E0"),sQuery(id+"F0.wireOp",EDGE,"E2.0"),sQuery(id+"F0.wireOp",EDGE,"E2.2"),sQuery(id+"F0.wireOp",EDGE,"E2.4"),subQ0,sQuery(id+"F0.wireOp",EDGE,"E14.2"),sQuery(id+"F0.wireOp",EDGE,"E14.3"),sQuery(id+"F0.wireOp",EDGE,"E14.4"),sQuery(id+"F0.wireOp",EDGE,"E14.5"),sQuery(id+"F0.wireOp",EDGE,"E15.1"),sQuery(id+"F0.wireOp",EDGE,"E15.2"),sQuery(id+"F0.wireOp",EDGE,"E15.3"),sQuery(id+"F0.wireOp",EDGE,"E15.4"),sQuery(id+"F0.wireOp",EDGE,"E15.5"),sQuery(id+"F0.wireOp",EDGE,"E19.1"),sQuery(id+"F0.wireOp",EDGE,"E19.2"),sQuery(id+"F0.wireOp",EDGE,"E19.3"),sQuery(id+"F0.wireOp",EDGE,"E19.4"),sQuery(id+"F0.wireOp",EDGE,"E19.5")])],"isStart":false})],"blendedInto":[makeQuery(id+"F1.opExtrude","CAP_FACE",FACE,{"disambiguationData":[OSD([sQuery(id+"F0.wireOp",EDGE,"E0"),sQuery(id+"F0.wireOp",EDGE,"E2.0"),sQuery(id+"F0.wireOp",EDGE,"E2.2"),sQuery(id+"F0.wireOp",EDGE,"E2.4"),subQ0,sQuery(id+"F0.wireOp",EDGE,"E14.2"),sQuery(id+"F0.wireOp",EDGE,"E14.3"),sQuery(id+"F0.wireOp",EDGE,"E14.4"),sQuery(id+"F0.wireOp",EDGE,"E14.5"),sQuery(id+"F0.wireOp",EDGE,"E15.1"),sQuery(id+"F0.wireOp",EDGE,"E15.2"),sQuery(id+"F0.wireOp",EDGE,"E15.3"),sQuery(id+"F0.wireOp",EDGE,"E15.4"),sQuery(id+"F0.wireOp",EDGE,"E15.5"),sQuery(id+"F0.wireOp",EDGE,"E19.1"),sQuery(id+"F0.wireOp",EDGE,"E19.2"),sQuery(id+"F0.wireOp",EDGE,"E19.3"),sQuery(id+"F0.wireOp",EDGE,"E19.4"),sQuery(id+"F0.wireOp",EDGE,"E19.5")])],"isStart":false})]});}
            var Q11;
            {var subQ0=sQuery(id+"F0.wireOp",EDGE,"E14.2");Q11=makeQuery(id+"F2.opChamfer","BLEND_EDGE",EDGE,{"blendedFrom":[makeQuery(id+"F1.opExtrude","CAP_EDGE",EDGE,{"disambiguationData":[OSD([subQ0])],"isStart":false}),makeQuery(id+"F1.opExtrude","CAP_FACE",FACE,{"disambiguationData":[OSD([sQuery(id+"F0.wireOp",EDGE,"E0"),sQuery(id+"F0.wireOp",EDGE,"E2.0"),sQuery(id+"F0.wireOp",EDGE,"E2.2"),sQuery(id+"F0.wireOp",EDGE,"E2.4"),sQuery(id+"F0.wireOp",EDGE,"E14.1"),subQ0,sQuery(id+"F0.wireOp",EDGE,"E14.3"),sQuery(id+"F0.wireOp",EDGE,"E14.4"),sQuery(id+"F0.wireOp",EDGE,"E14.5"),sQuery(id+"F0.wireOp",EDGE,"E15.1"),sQuery(id+"F0.wireOp",EDGE,"E15.2"),sQuery(id+"F0.wireOp",EDGE,"E15.3"),sQuery(id+"F0.wireOp",EDGE,"E15.4"),sQuery(id+"F0.wireOp",EDGE,"E15.5"),sQuery(id+"F0.wireOp",EDGE,"E19.1"),sQuery(id+"F0.wireOp",EDGE,"E19.2"),sQuery(id+"F0.wireOp",EDGE,"E19.3"),sQuery(id+"F0.wireOp",EDGE,"E19.4"),sQuery(id+"F0.wireOp",EDGE,"E19.5")])],"isStart":false})],"blendedInto":[makeQuery(id+"F1.opExtrude","CAP_FACE",FACE,{"disambiguationData":[OSD([sQuery(id+"F0.wireOp",EDGE,"E0"),sQuery(id+"F0.wireOp",EDGE,"E2.0"),sQuery(id+"F0.wireOp",EDGE,"E2.2"),sQuery(id+"F0.wireOp",EDGE,"E2.4"),sQuery(id+"F0.wireOp",EDGE,"E14.1"),subQ0,sQuery(id+"F0.wireOp",EDGE,"E14.3"),sQuery(id+"F0.wireOp",EDGE,"E14.4"),sQuery(id+"F0.wireOp",EDGE,"E14.5"),sQuery(id+"F0.wireOp",EDGE,"E15.1"),sQuery(id+"F0.wireOp",EDGE,"E15.2"),sQuery(id+"F0.wireOp",EDGE,"E15.3"),sQuery(id+"F0.wireOp",EDGE,"E15.4"),sQuery(id+"F0.wireOp",EDGE,"E15.5"),sQuery(id+"F0.wireOp",EDGE,"E19.1"),sQuery(id+"F0.wireOp",EDGE,"E19.2"),sQuery(id+"F0.wireOp",EDGE,"E19.3"),sQuery(id+"F0.wireOp",EDGE,"E19.4"),sQuery(id+"F0.wireOp",EDGE,"E19.5")])],"isStart":false})]});}
            chamfer(context, id + "F5", {"entities" : qUnion([Q0, Q1, Q2, Q3, Q4, Q5, Q6, Q7, Q8, Q9, Q10, Q11]), "width" : 3 * mm, "tangentPropagation" : true});
        }
        {
            var Q0;
            {var subQ0=sQuery(id+"F0.wireOp",EDGE,"E19.4");var subQ1=makeQuery(id+"F1.opExtrude","CAP_FACE",FACE,{"disambiguationData":[OSD([sQuery(id+"F0.wireOp",EDGE,"E0"),sQuery(id+"F0.wireOp",EDGE,"E2.0"),sQuery(id+"F0.wireOp",EDGE,"E2.2"),sQuery(id+"F0.wireOp",EDGE,"E2.4"),sQuery(id+"F0.wireOp",EDGE,"E14.1"),sQuery(id+"F0.wireOp",EDGE,"E14.2"),sQuery(id+"F0.wireOp",EDGE,"E14.3"),sQuery(id+"F0.wireOp",EDGE,"E14.4"),sQuery(id+"F0.wireOp",EDGE,"E14.5"),sQuery(id+"F0.wireOp",EDGE,"E15.1"),sQuery(id+"F0.wireOp",EDGE,"E15.2"),sQuery(id+"F0.wireOp",EDGE,"E15.3"),sQuery(id+"F0.wireOp",EDGE,"E15.4"),sQuery(id+"F0.wireOp",EDGE,"E15.5"),sQuery(id+"F0.wireOp",EDGE,"E19.1"),sQuery(id+"F0.wireOp",EDGE,"E19.2"),sQuery(id+"F0.wireOp",EDGE,"E19.3"),subQ0,sQuery(id+"F0.wireOp",EDGE,"E19.5")])],"isStart":false});Q0=makeQuery(id+"F5.opChamfer","BLEND_EDGE",EDGE,{"blendedFrom":[makeQuery(id+"F2.opChamfer","BLEND_EDGE",EDGE,{"blendedFrom":[makeQuery(id+"F1.opExtrude","CAP_EDGE",EDGE,{"disambiguationData":[OSD([subQ0])],"isStart":false}),subQ1],"blendedInto":[subQ1]}),subQ1],"blendedInto":[subQ1]});}
            var Q1;
            {var subQ0=sQuery(id+"F0.wireOp",EDGE,"E19.5");var subQ1=makeQuery(id+"F1.opExtrude","CAP_FACE",FACE,{"disambiguationData":[OSD([sQuery(id+"F0.wireOp",EDGE,"E0"),sQuery(id+"F0.wireOp",EDGE,"E2.0"),sQuery(id+"F0.wireOp",EDGE,"E2.2"),sQuery(id+"F0.wireOp",EDGE,"E2.4"),sQuery(id+"F0.wireOp",EDGE,"E14.1"),sQuery(id+"F0.wireOp",EDGE,"E14.2"),sQuery(id+"F0.wireOp",EDGE,"E14.3"),sQuery(id+"F0.wireOp",EDGE,"E14.4"),sQuery(id+"F0.wireOp",EDGE,"E14.5"),sQuery(id+"F0.wireOp",EDGE,"E15.1"),sQuery(id+"F0.wireOp",EDGE,"E15.2"),sQuery(id+"F0.wireOp",EDGE,"E15.3"),sQuery(id+"F0.wireOp",EDGE,"E15.4"),sQuery(id+"F0.wireOp",EDGE,"E15.5"),sQuery(id+"F0.wireOp",EDGE,"E19.1"),sQuery(id+"F0.wireOp",EDGE,"E19.2"),sQuery(id+"F0.wireOp",EDGE,"E19.3"),sQuery(id+"F0.wireOp",EDGE,"E19.4"),subQ0])],"isStart":false});Q1=makeQuery(id+"F5.opChamfer","BLEND_EDGE",EDGE,{"blendedFrom":[makeQuery(id+"F2.opChamfer","BLEND_EDGE",EDGE,{"blendedFrom":[makeQuery(id+"F1.opExtrude","CAP_EDGE",EDGE,{"disambiguationData":[OSD([subQ0])],"isStart":false}),subQ1],"blendedInto":[subQ1]}),subQ1],"blendedInto":[subQ1]});}
            var Q2;
            {var subQ0=sQuery(id+"F0.wireOp",EDGE,"E19.2");var subQ1=makeQuery(id+"F1.opExtrude","CAP_FACE",FACE,{"disambiguationData":[OSD([sQuery(id+"F0.wireOp",EDGE,"E0"),sQuery(id+"F0.wireOp",EDGE,"E2.0"),sQuery(id+"F0.wireOp",EDGE,"E2.2"),sQuery(id+"F0.wireOp",EDGE,"E2.4"),sQuery(id+"F0.wireOp",EDGE,"E14.1"),sQuery(id+"F0.wireOp",EDGE,"E14.2"),sQuery(id+"F0.wireOp",EDGE,"E14.3"),sQuery(id+"F0.wireOp",EDGE,"E14.4"),sQuery(id+"F0.wireOp",EDGE,"E14.5"),sQuery(id+"F0.wireOp",EDGE,"E15.1"),sQuery(id+"F0.wireOp",EDGE,"E15.2"),sQuery(id+"F0.wireOp",EDGE,"E15.3"),sQuery(id+"F0.wireOp",EDGE,"E15.4"),sQuery(id+"F0.wireOp",EDGE,"E15.5"),sQuery(id+"F0.wireOp",EDGE,"E19.1"),subQ0,sQuery(id+"F0.wireOp",EDGE,"E19.3"),sQuery(id+"F0.wireOp",EDGE,"E19.4"),sQuery(id+"F0.wireOp",EDGE,"E19.5")])],"isStart":false});Q2=makeQuery(id+"F5.opChamfer","BLEND_EDGE",EDGE,{"blendedFrom":[makeQuery(id+"F2.opChamfer","BLEND_EDGE",EDGE,{"blendedFrom":[makeQuery(id+"F1.opExtrude","CAP_EDGE",EDGE,{"disambiguationData":[OSD([subQ0])],"isStart":false}),subQ1],"blendedInto":[subQ1]}),subQ1],"blendedInto":[subQ1]});}
            var Q3;
            {var subQ0=sQuery(id+"F0.wireOp",EDGE,"E19.1");var subQ1=makeQuery(id+"F1.opExtrude","CAP_FACE",FACE,{"disambiguationData":[OSD([sQuery(id+"F0.wireOp",EDGE,"E0"),sQuery(id+"F0.wireOp",EDGE,"E2.0"),sQuery(id+"F0.wireOp",EDGE,"E2.2"),sQuery(id+"F0.wireOp",EDGE,"E2.4"),sQuery(id+"F0.wireOp",EDGE,"E14.1"),sQuery(id+"F0.wireOp",EDGE,"E14.2"),sQuery(id+"F0.wireOp",EDGE,"E14.3"),sQuery(id+"F0.wireOp",EDGE,"E14.4"),sQuery(id+"F0.wireOp",EDGE,"E14.5"),sQuery(id+"F0.wireOp",EDGE,"E15.1"),sQuery(id+"F0.wireOp",EDGE,"E15.2"),sQuery(id+"F0.wireOp",EDGE,"E15.3"),sQuery(id+"F0.wireOp",EDGE,"E15.4"),sQuery(id+"F0.wireOp",EDGE,"E15.5"),subQ0,sQuery(id+"F0.wireOp",EDGE,"E19.2"),sQuery(id+"F0.wireOp",EDGE,"E19.3"),sQuery(id+"F0.wireOp",EDGE,"E19.4"),sQuery(id+"F0.wireOp",EDGE,"E19.5")])],"isStart":false});Q3=makeQuery(id+"F5.opChamfer","BLEND_EDGE",EDGE,{"blendedFrom":[makeQuery(id+"F2.opChamfer","BLEND_EDGE",EDGE,{"blendedFrom":[makeQuery(id+"F1.opExtrude","CAP_EDGE",EDGE,{"disambiguationData":[OSD([subQ0])],"isStart":false}),subQ1],"blendedInto":[subQ1]}),subQ1],"blendedInto":[subQ1]});}
            var Q4;
            {var subQ0=sQuery(id+"F0.wireOp",EDGE,"E15.1");var subQ1=makeQuery(id+"F1.opExtrude","CAP_FACE",FACE,{"disambiguationData":[OSD([sQuery(id+"F0.wireOp",EDGE,"E0"),sQuery(id+"F0.wireOp",EDGE,"E2.0"),sQuery(id+"F0.wireOp",EDGE,"E2.2"),sQuery(id+"F0.wireOp",EDGE,"E2.4"),sQuery(id+"F0.wireOp",EDGE,"E14.1"),sQuery(id+"F0.wireOp",EDGE,"E14.2"),sQuery(id+"F0.wireOp",EDGE,"E14.3"),sQuery(id+"F0.wireOp",EDGE,"E14.4"),sQuery(id+"F0.wireOp",EDGE,"E14.5"),subQ0,sQuery(id+"F0.wireOp",EDGE,"E15.2"),sQuery(id+"F0.wireOp",EDGE,"E15.3"),sQuery(id+"F0.wireOp",EDGE,"E15.4"),sQuery(id+"F0.wireOp",EDGE,"E15.5"),sQuery(id+"F0.wireOp",EDGE,"E19.1"),sQuery(id+"F0.wireOp",EDGE,"E19.2"),sQuery(id+"F0.wireOp",EDGE,"E19.3"),sQuery(id+"F0.wireOp",EDGE,"E19.4"),sQuery(id+"F0.wireOp",EDGE,"E19.5")])],"isStart":false});Q4=makeQuery(id+"F5.opChamfer","BLEND_EDGE",EDGE,{"blendedFrom":[makeQuery(id+"F3.opChamfer","BLEND_EDGE",EDGE,{"blendedFrom":[makeQuery(id+"F1.opExtrude","CAP_EDGE",EDGE,{"disambiguationData":[OSD([subQ0])],"isStart":false}),subQ1],"blendedInto":[subQ1]}),subQ1],"blendedInto":[subQ1]});}
            var Q5;
            {var subQ0=sQuery(id+"F0.wireOp",EDGE,"E15.2");var subQ1=makeQuery(id+"F1.opExtrude","CAP_FACE",FACE,{"disambiguationData":[OSD([sQuery(id+"F0.wireOp",EDGE,"E0"),sQuery(id+"F0.wireOp",EDGE,"E2.0"),sQuery(id+"F0.wireOp",EDGE,"E2.2"),sQuery(id+"F0.wireOp",EDGE,"E2.4"),sQuery(id+"F0.wireOp",EDGE,"E14.1"),sQuery(id+"F0.wireOp",EDGE,"E14.2"),sQuery(id+"F0.wireOp",EDGE,"E14.3"),sQuery(id+"F0.wireOp",EDGE,"E14.4"),sQuery(id+"F0.wireOp",EDGE,"E14.5"),sQuery(id+"F0.wireOp",EDGE,"E15.1"),subQ0,sQuery(id+"F0.wireOp",EDGE,"E15.3"),sQuery(id+"F0.wireOp",EDGE,"E15.4"),sQuery(id+"F0.wireOp",EDGE,"E15.5"),sQuery(id+"F0.wireOp",EDGE,"E19.1"),sQuery(id+"F0.wireOp",EDGE,"E19.2"),sQuery(id+"F0.wireOp",EDGE,"E19.3"),sQuery(id+"F0.wireOp",EDGE,"E19.4"),sQuery(id+"F0.wireOp",EDGE,"E19.5")])],"isStart":false});Q5=makeQuery(id+"F5.opChamfer","BLEND_EDGE",EDGE,{"blendedFrom":[makeQuery(id+"F2.opChamfer","BLEND_EDGE",EDGE,{"blendedFrom":[makeQuery(id+"F1.opExtrude","CAP_EDGE",EDGE,{"disambiguationData":[OSD([subQ0])],"isStart":false}),subQ1],"blendedInto":[subQ1]}),subQ1],"blendedInto":[subQ1]});}
            var Q6;
            {var subQ0=sQuery(id+"F0.wireOp",EDGE,"E15.4");var subQ1=makeQuery(id+"F1.opExtrude","CAP_FACE",FACE,{"disambiguationData":[OSD([sQuery(id+"F0.wireOp",EDGE,"E0"),sQuery(id+"F0.wireOp",EDGE,"E2.0"),sQuery(id+"F0.wireOp",EDGE,"E2.2"),sQuery(id+"F0.wireOp",EDGE,"E2.4"),sQuery(id+"F0.wireOp",EDGE,"E14.1"),sQuery(id+"F0.wireOp",EDGE,"E14.2"),sQuery(id+"F0.wireOp",EDGE,"E14.3"),sQuery(id+"F0.wireOp",EDGE,"E14.4"),sQuery(id+"F0.wireOp",EDGE,"E14.5"),sQuery(id+"F0.wireOp",EDGE,"E15.1"),sQuery(id+"F0.wireOp",EDGE,"E15.2"),sQuery(id+"F0.wireOp",EDGE,"E15.3"),subQ0,sQuery(id+"F0.wireOp",EDGE,"E15.5"),sQuery(id+"F0.wireOp",EDGE,"E19.1"),sQuery(id+"F0.wireOp",EDGE,"E19.2"),sQuery(id+"F0.wireOp",EDGE,"E19.3"),sQuery(id+"F0.wireOp",EDGE,"E19.4"),sQuery(id+"F0.wireOp",EDGE,"E19.5")])],"isStart":false});Q6=makeQuery(id+"F5.opChamfer","BLEND_EDGE",EDGE,{"blendedFrom":[makeQuery(id+"F2.opChamfer","BLEND_EDGE",EDGE,{"blendedFrom":[makeQuery(id+"F1.opExtrude","CAP_EDGE",EDGE,{"disambiguationData":[OSD([subQ0])],"isStart":false}),subQ1],"blendedInto":[subQ1]}),subQ1],"blendedInto":[subQ1]});}
            var Q7;
            {var subQ0=sQuery(id+"F0.wireOp",EDGE,"E15.5");var subQ1=makeQuery(id+"F1.opExtrude","CAP_FACE",FACE,{"disambiguationData":[OSD([sQuery(id+"F0.wireOp",EDGE,"E0"),sQuery(id+"F0.wireOp",EDGE,"E2.0"),sQuery(id+"F0.wireOp",EDGE,"E2.2"),sQuery(id+"F0.wireOp",EDGE,"E2.4"),sQuery(id+"F0.wireOp",EDGE,"E14.1"),sQuery(id+"F0.wireOp",EDGE,"E14.2"),sQuery(id+"F0.wireOp",EDGE,"E14.3"),sQuery(id+"F0.wireOp",EDGE,"E14.4"),sQuery(id+"F0.wireOp",EDGE,"E14.5"),sQuery(id+"F0.wireOp",EDGE,"E15.1"),sQuery(id+"F0.wireOp",EDGE,"E15.2"),sQuery(id+"F0.wireOp",EDGE,"E15.3"),sQuery(id+"F0.wireOp",EDGE,"E15.4"),subQ0,sQuery(id+"F0.wireOp",EDGE,"E19.1"),sQuery(id+"F0.wireOp",EDGE,"E19.2"),sQuery(id+"F0.wireOp",EDGE,"E19.3"),sQuery(id+"F0.wireOp",EDGE,"E19.4"),sQuery(id+"F0.wireOp",EDGE,"E19.5")])],"isStart":false});Q7=makeQuery(id+"F5.opChamfer","BLEND_EDGE",EDGE,{"blendedFrom":[makeQuery(id+"F2.opChamfer","BLEND_EDGE",EDGE,{"blendedFrom":[makeQuery(id+"F1.opExtrude","CAP_EDGE",EDGE,{"disambiguationData":[OSD([subQ0])],"isStart":false}),subQ1],"blendedInto":[subQ1]}),subQ1],"blendedInto":[subQ1]});}
            var Q8;
            {var subQ0=sQuery(id+"F0.wireOp",EDGE,"E14.1");var subQ1=makeQuery(id+"F1.opExtrude","CAP_FACE",FACE,{"disambiguationData":[OSD([sQuery(id+"F0.wireOp",EDGE,"E0"),sQuery(id+"F0.wireOp",EDGE,"E2.0"),sQuery(id+"F0.wireOp",EDGE,"E2.2"),sQuery(id+"F0.wireOp",EDGE,"E2.4"),subQ0,sQuery(id+"F0.wireOp",EDGE,"E14.2"),sQuery(id+"F0.wireOp",EDGE,"E14.3"),sQuery(id+"F0.wireOp",EDGE,"E14.4"),sQuery(id+"F0.wireOp",EDGE,"E14.5"),sQuery(id+"F0.wireOp",EDGE,"E15.1"),sQuery(id+"F0.wireOp",EDGE,"E15.2"),sQuery(id+"F0.wireOp",EDGE,"E15.3"),sQuery(id+"F0.wireOp",EDGE,"E15.4"),sQuery(id+"F0.wireOp",EDGE,"E15.5"),sQuery(id+"F0.wireOp",EDGE,"E19.1"),sQuery(id+"F0.wireOp",EDGE,"E19.2"),sQuery(id+"F0.wireOp",EDGE,"E19.3"),sQuery(id+"F0.wireOp",EDGE,"E19.4"),sQuery(id+"F0.wireOp",EDGE,"E19.5")])],"isStart":false});Q8=makeQuery(id+"F5.opChamfer","BLEND_EDGE",EDGE,{"blendedFrom":[makeQuery(id+"F2.opChamfer","BLEND_EDGE",EDGE,{"blendedFrom":[makeQuery(id+"F1.opExtrude","CAP_EDGE",EDGE,{"disambiguationData":[OSD([subQ0])],"isStart":false}),subQ1],"blendedInto":[subQ1]}),subQ1],"blendedInto":[subQ1]});}
            var Q9;
            {var subQ0=sQuery(id+"F0.wireOp",EDGE,"E14.2");var subQ1=makeQuery(id+"F1.opExtrude","CAP_FACE",FACE,{"disambiguationData":[OSD([sQuery(id+"F0.wireOp",EDGE,"E0"),sQuery(id+"F0.wireOp",EDGE,"E2.0"),sQuery(id+"F0.wireOp",EDGE,"E2.2"),sQuery(id+"F0.wireOp",EDGE,"E2.4"),sQuery(id+"F0.wireOp",EDGE,"E14.1"),subQ0,sQuery(id+"F0.wireOp",EDGE,"E14.3"),sQuery(id+"F0.wireOp",EDGE,"E14.4"),sQuery(id+"F0.wireOp",EDGE,"E14.5"),sQuery(id+"F0.wireOp",EDGE,"E15.1"),sQuery(id+"F0.wireOp",EDGE,"E15.2"),sQuery(id+"F0.wireOp",EDGE,"E15.3"),sQuery(id+"F0.wireOp",EDGE,"E15.4"),sQuery(id+"F0.wireOp",EDGE,"E15.5"),sQuery(id+"F0.wireOp",EDGE,"E19.1"),sQuery(id+"F0.wireOp",EDGE,"E19.2"),sQuery(id+"F0.wireOp",EDGE,"E19.3"),sQuery(id+"F0.wireOp",EDGE,"E19.4"),sQuery(id+"F0.wireOp",EDGE,"E19.5")])],"isStart":false});Q9=makeQuery(id+"F5.opChamfer","BLEND_EDGE",EDGE,{"blendedFrom":[makeQuery(id+"F2.opChamfer","BLEND_EDGE",EDGE,{"blendedFrom":[makeQuery(id+"F1.opExtrude","CAP_EDGE",EDGE,{"disambiguationData":[OSD([subQ0])],"isStart":false}),subQ1],"blendedInto":[subQ1]}),subQ1],"blendedInto":[subQ1]});}
            var Q10;
            {var subQ0=sQuery(id+"F0.wireOp",EDGE,"E14.5");var subQ1=makeQuery(id+"F1.opExtrude","CAP_FACE",FACE,{"disambiguationData":[OSD([sQuery(id+"F0.wireOp",EDGE,"E0"),sQuery(id+"F0.wireOp",EDGE,"E2.0"),sQuery(id+"F0.wireOp",EDGE,"E2.2"),sQuery(id+"F0.wireOp",EDGE,"E2.4"),sQuery(id+"F0.wireOp",EDGE,"E14.1"),sQuery(id+"F0.wireOp",EDGE,"E14.2"),sQuery(id+"F0.wireOp",EDGE,"E14.3"),sQuery(id+"F0.wireOp",EDGE,"E14.4"),subQ0,sQuery(id+"F0.wireOp",EDGE,"E15.1"),sQuery(id+"F0.wireOp",EDGE,"E15.2"),sQuery(id+"F0.wireOp",EDGE,"E15.3"),sQuery(id+"F0.wireOp",EDGE,"E15.4"),sQuery(id+"F0.wireOp",EDGE,"E15.5"),sQuery(id+"F0.wireOp",EDGE,"E19.1"),sQuery(id+"F0.wireOp",EDGE,"E19.2"),sQuery(id+"F0.wireOp",EDGE,"E19.3"),sQuery(id+"F0.wireOp",EDGE,"E19.4"),sQuery(id+"F0.wireOp",EDGE,"E19.5")])],"isStart":false});Q10=makeQuery(id+"F5.opChamfer","BLEND_EDGE",EDGE,{"blendedFrom":[makeQuery(id+"F2.opChamfer","BLEND_EDGE",EDGE,{"blendedFrom":[makeQuery(id+"F1.opExtrude","CAP_EDGE",EDGE,{"disambiguationData":[OSD([subQ0])],"isStart":false}),subQ1],"blendedInto":[subQ1]}),subQ1],"blendedInto":[subQ1]});}
            var Q11;
            {var subQ0=sQuery(id+"F0.wireOp",EDGE,"E14.4");var subQ1=makeQuery(id+"F1.opExtrude","CAP_FACE",FACE,{"disambiguationData":[OSD([sQuery(id+"F0.wireOp",EDGE,"E0"),sQuery(id+"F0.wireOp",EDGE,"E2.0"),sQuery(id+"F0.wireOp",EDGE,"E2.2"),sQuery(id+"F0.wireOp",EDGE,"E2.4"),sQuery(id+"F0.wireOp",EDGE,"E14.1"),sQuery(id+"F0.wireOp",EDGE,"E14.2"),sQuery(id+"F0.wireOp",EDGE,"E14.3"),subQ0,sQuery(id+"F0.wireOp",EDGE,"E14.5"),sQuery(id+"F0.wireOp",EDGE,"E15.1"),sQuery(id+"F0.wireOp",EDGE,"E15.2"),sQuery(id+"F0.wireOp",EDGE,"E15.3"),sQuery(id+"F0.wireOp",EDGE,"E15.4"),sQuery(id+"F0.wireOp",EDGE,"E15.5"),sQuery(id+"F0.wireOp",EDGE,"E19.1"),sQuery(id+"F0.wireOp",EDGE,"E19.2"),sQuery(id+"F0.wireOp",EDGE,"E19.3"),sQuery(id+"F0.wireOp",EDGE,"E19.4"),sQuery(id+"F0.wireOp",EDGE,"E19.5")])],"isStart":false});Q11=makeQuery(id+"F5.opChamfer","BLEND_EDGE",EDGE,{"blendedFrom":[makeQuery(id+"F2.opChamfer","BLEND_EDGE",EDGE,{"blendedFrom":[makeQuery(id+"F1.opExtrude","CAP_EDGE",EDGE,{"disambiguationData":[OSD([subQ0])],"isStart":false}),subQ1],"blendedInto":[subQ1]}),subQ1],"blendedInto":[subQ1]});}
            chamfer(context, id + "F6", {"entities" : qUnion([Q0, Q1, Q2, Q3, Q4, Q5, Q6, Q7, Q8, Q9, Q10, Q11]), "width" : 2.5 * mm, "tangentPropagation" : true});
        }
        {
            var Q0;
            {var subQ0=sQuery(id+"F0.wireOp",EDGE,"E15.4");Q0=makeQuery(id+"F2.opChamfer","BLEND_EDGE",EDGE,{"blendedFrom":[makeQuery(id+"F1.opExtrude","CAP_EDGE",EDGE,{"disambiguationData":[OSD([subQ0])],"isStart":true}),makeQuery(id+"F1.opExtrude","CAP_FACE",FACE,{"disambiguationData":[OSD([sQuery(id+"F0.wireOp",EDGE,"E0"),sQuery(id+"F0.wireOp",EDGE,"E2.0"),sQuery(id+"F0.wireOp",EDGE,"E2.2"),sQuery(id+"F0.wireOp",EDGE,"E2.4"),sQuery(id+"F0.wireOp",EDGE,"E14.1"),sQuery(id+"F0.wireOp",EDGE,"E14.2"),sQuery(id+"F0.wireOp",EDGE,"E14.3"),sQuery(id+"F0.wireOp",EDGE,"E14.4"),sQuery(id+"F0.wireOp",EDGE,"E14.5"),sQuery(id+"F0.wireOp",EDGE,"E15.1"),sQuery(id+"F0.wireOp",EDGE,"E15.2"),sQuery(id+"F0.wireOp",EDGE,"E15.3"),subQ0,sQuery(id+"F0.wireOp",EDGE,"E15.5"),sQuery(id+"F0.wireOp",EDGE,"E19.1"),sQuery(id+"F0.wireOp",EDGE,"E19.2"),sQuery(id+"F0.wireOp",EDGE,"E19.3"),sQuery(id+"F0.wireOp",EDGE,"E19.4"),sQuery(id+"F0.wireOp",EDGE,"E19.5")])],"isStart":true})],"blendedInto":[makeQuery(id+"F1.opExtrude","CAP_FACE",FACE,{"disambiguationData":[OSD([sQuery(id+"F0.wireOp",EDGE,"E0"),sQuery(id+"F0.wireOp",EDGE,"E2.0"),sQuery(id+"F0.wireOp",EDGE,"E2.2"),sQuery(id+"F0.wireOp",EDGE,"E2.4"),sQuery(id+"F0.wireOp",EDGE,"E14.1"),sQuery(id+"F0.wireOp",EDGE,"E14.2"),sQuery(id+"F0.wireOp",EDGE,"E14.3"),sQuery(id+"F0.wireOp",EDGE,"E14.4"),sQuery(id+"F0.wireOp",EDGE,"E14.5"),sQuery(id+"F0.wireOp",EDGE,"E15.1"),sQuery(id+"F0.wireOp",EDGE,"E15.2"),sQuery(id+"F0.wireOp",EDGE,"E15.3"),subQ0,sQuery(id+"F0.wireOp",EDGE,"E15.5"),sQuery(id+"F0.wireOp",EDGE,"E19.1"),sQuery(id+"F0.wireOp",EDGE,"E19.2"),sQuery(id+"F0.wireOp",EDGE,"E19.3"),sQuery(id+"F0.wireOp",EDGE,"E19.4"),sQuery(id+"F0.wireOp",EDGE,"E19.5")])],"isStart":true})]});}
            var Q1;
            {var subQ0=sQuery(id+"F0.wireOp",EDGE,"E15.2");Q1=makeQuery(id+"F2.opChamfer","BLEND_EDGE",EDGE,{"blendedFrom":[makeQuery(id+"F1.opExtrude","CAP_EDGE",EDGE,{"disambiguationData":[OSD([subQ0])],"isStart":true}),makeQuery(id+"F1.opExtrude","CAP_FACE",FACE,{"disambiguationData":[OSD([sQuery(id+"F0.wireOp",EDGE,"E0"),sQuery(id+"F0.wireOp",EDGE,"E2.0"),sQuery(id+"F0.wireOp",EDGE,"E2.2"),sQuery(id+"F0.wireOp",EDGE,"E2.4"),sQuery(id+"F0.wireOp",EDGE,"E14.1"),sQuery(id+"F0.wireOp",EDGE,"E14.2"),sQuery(id+"F0.wireOp",EDGE,"E14.3"),sQuery(id+"F0.wireOp",EDGE,"E14.4"),sQuery(id+"F0.wireOp",EDGE,"E14.5"),sQuery(id+"F0.wireOp",EDGE,"E15.1"),subQ0,sQuery(id+"F0.wireOp",EDGE,"E15.3"),sQuery(id+"F0.wireOp",EDGE,"E15.4"),sQuery(id+"F0.wireOp",EDGE,"E15.5"),sQuery(id+"F0.wireOp",EDGE,"E19.1"),sQuery(id+"F0.wireOp",EDGE,"E19.2"),sQuery(id+"F0.wireOp",EDGE,"E19.3"),sQuery(id+"F0.wireOp",EDGE,"E19.4"),sQuery(id+"F0.wireOp",EDGE,"E19.5")])],"isStart":true})],"blendedInto":[makeQuery(id+"F1.opExtrude","CAP_FACE",FACE,{"disambiguationData":[OSD([sQuery(id+"F0.wireOp",EDGE,"E0"),sQuery(id+"F0.wireOp",EDGE,"E2.0"),sQuery(id+"F0.wireOp",EDGE,"E2.2"),sQuery(id+"F0.wireOp",EDGE,"E2.4"),sQuery(id+"F0.wireOp",EDGE,"E14.1"),sQuery(id+"F0.wireOp",EDGE,"E14.2"),sQuery(id+"F0.wireOp",EDGE,"E14.3"),sQuery(id+"F0.wireOp",EDGE,"E14.4"),sQuery(id+"F0.wireOp",EDGE,"E14.5"),sQuery(id+"F0.wireOp",EDGE,"E15.1"),subQ0,sQuery(id+"F0.wireOp",EDGE,"E15.3"),sQuery(id+"F0.wireOp",EDGE,"E15.4"),sQuery(id+"F0.wireOp",EDGE,"E15.5"),sQuery(id+"F0.wireOp",EDGE,"E19.1"),sQuery(id+"F0.wireOp",EDGE,"E19.2"),sQuery(id+"F0.wireOp",EDGE,"E19.3"),sQuery(id+"F0.wireOp",EDGE,"E19.4"),sQuery(id+"F0.wireOp",EDGE,"E19.5")])],"isStart":true})]});}
            var Q2;
            {var subQ0=sQuery(id+"F0.wireOp",EDGE,"E15.1");Q2=makeQuery(id+"F2.opChamfer","BLEND_EDGE",EDGE,{"blendedFrom":[makeQuery(id+"F1.opExtrude","CAP_EDGE",EDGE,{"disambiguationData":[OSD([subQ0])],"isStart":true}),makeQuery(id+"F1.opExtrude","CAP_FACE",FACE,{"disambiguationData":[OSD([sQuery(id+"F0.wireOp",EDGE,"E0"),sQuery(id+"F0.wireOp",EDGE,"E2.0"),sQuery(id+"F0.wireOp",EDGE,"E2.2"),sQuery(id+"F0.wireOp",EDGE,"E2.4"),sQuery(id+"F0.wireOp",EDGE,"E14.1"),sQuery(id+"F0.wireOp",EDGE,"E14.2"),sQuery(id+"F0.wireOp",EDGE,"E14.3"),sQuery(id+"F0.wireOp",EDGE,"E14.4"),sQuery(id+"F0.wireOp",EDGE,"E14.5"),subQ0,sQuery(id+"F0.wireOp",EDGE,"E15.2"),sQuery(id+"F0.wireOp",EDGE,"E15.3"),sQuery(id+"F0.wireOp",EDGE,"E15.4"),sQuery(id+"F0.wireOp",EDGE,"E15.5"),sQuery(id+"F0.wireOp",EDGE,"E19.1"),sQuery(id+"F0.wireOp",EDGE,"E19.2"),sQuery(id+"F0.wireOp",EDGE,"E19.3"),sQuery(id+"F0.wireOp",EDGE,"E19.4"),sQuery(id+"F0.wireOp",EDGE,"E19.5")])],"isStart":true})],"blendedInto":[makeQuery(id+"F1.opExtrude","CAP_FACE",FACE,{"disambiguationData":[OSD([sQuery(id+"F0.wireOp",EDGE,"E0"),sQuery(id+"F0.wireOp",EDGE,"E2.0"),sQuery(id+"F0.wireOp",EDGE,"E2.2"),sQuery(id+"F0.wireOp",EDGE,"E2.4"),sQuery(id+"F0.wireOp",EDGE,"E14.1"),sQuery(id+"F0.wireOp",EDGE,"E14.2"),sQuery(id+"F0.wireOp",EDGE,"E14.3"),sQuery(id+"F0.wireOp",EDGE,"E14.4"),sQuery(id+"F0.wireOp",EDGE,"E14.5"),subQ0,sQuery(id+"F0.wireOp",EDGE,"E15.2"),sQuery(id+"F0.wireOp",EDGE,"E15.3"),sQuery(id+"F0.wireOp",EDGE,"E15.4"),sQuery(id+"F0.wireOp",EDGE,"E15.5"),sQuery(id+"F0.wireOp",EDGE,"E19.1"),sQuery(id+"F0.wireOp",EDGE,"E19.2"),sQuery(id+"F0.wireOp",EDGE,"E19.3"),sQuery(id+"F0.wireOp",EDGE,"E19.4"),sQuery(id+"F0.wireOp",EDGE,"E19.5")])],"isStart":true})]});}
            var Q3;
            {var subQ0=sQuery(id+"F0.wireOp",EDGE,"E15.5");Q3=makeQuery(id+"F2.opChamfer","BLEND_EDGE",EDGE,{"blendedFrom":[makeQuery(id+"F1.opExtrude","CAP_EDGE",EDGE,{"disambiguationData":[OSD([subQ0])],"isStart":true}),makeQuery(id+"F1.opExtrude","CAP_FACE",FACE,{"disambiguationData":[OSD([sQuery(id+"F0.wireOp",EDGE,"E0"),sQuery(id+"F0.wireOp",EDGE,"E2.0"),sQuery(id+"F0.wireOp",EDGE,"E2.2"),sQuery(id+"F0.wireOp",EDGE,"E2.4"),sQuery(id+"F0.wireOp",EDGE,"E14.1"),sQuery(id+"F0.wireOp",EDGE,"E14.2"),sQuery(id+"F0.wireOp",EDGE,"E14.3"),sQuery(id+"F0.wireOp",EDGE,"E14.4"),sQuery(id+"F0.wireOp",EDGE,"E14.5"),sQuery(id+"F0.wireOp",EDGE,"E15.1"),sQuery(id+"F0.wireOp",EDGE,"E15.2"),sQuery(id+"F0.wireOp",EDGE,"E15.3"),sQuery(id+"F0.wireOp",EDGE,"E15.4"),subQ0,sQuery(id+"F0.wireOp",EDGE,"E19.1"),sQuery(id+"F0.wireOp",EDGE,"E19.2"),sQuery(id+"F0.wireOp",EDGE,"E19.3"),sQuery(id+"F0.wireOp",EDGE,"E19.4"),sQuery(id+"F0.wireOp",EDGE,"E19.5")])],"isStart":true})],"blendedInto":[makeQuery(id+"F1.opExtrude","CAP_FACE",FACE,{"disambiguationData":[OSD([sQuery(id+"F0.wireOp",EDGE,"E0"),sQuery(id+"F0.wireOp",EDGE,"E2.0"),sQuery(id+"F0.wireOp",EDGE,"E2.2"),sQuery(id+"F0.wireOp",EDGE,"E2.4"),sQuery(id+"F0.wireOp",EDGE,"E14.1"),sQuery(id+"F0.wireOp",EDGE,"E14.2"),sQuery(id+"F0.wireOp",EDGE,"E14.3"),sQuery(id+"F0.wireOp",EDGE,"E14.4"),sQuery(id+"F0.wireOp",EDGE,"E14.5"),sQuery(id+"F0.wireOp",EDGE,"E15.1"),sQuery(id+"F0.wireOp",EDGE,"E15.2"),sQuery(id+"F0.wireOp",EDGE,"E15.3"),sQuery(id+"F0.wireOp",EDGE,"E15.4"),subQ0,sQuery(id+"F0.wireOp",EDGE,"E19.1"),sQuery(id+"F0.wireOp",EDGE,"E19.2"),sQuery(id+"F0.wireOp",EDGE,"E19.3"),sQuery(id+"F0.wireOp",EDGE,"E19.4"),sQuery(id+"F0.wireOp",EDGE,"E19.5")])],"isStart":true})]});}
            var Q4;
            {var subQ0=sQuery(id+"F0.wireOp",EDGE,"E19.5");Q4=makeQuery(id+"F2.opChamfer","BLEND_EDGE",EDGE,{"blendedFrom":[makeQuery(id+"F1.opExtrude","CAP_EDGE",EDGE,{"disambiguationData":[OSD([subQ0])],"isStart":true}),makeQuery(id+"F1.opExtrude","CAP_FACE",FACE,{"disambiguationData":[OSD([sQuery(id+"F0.wireOp",EDGE,"E0"),sQuery(id+"F0.wireOp",EDGE,"E2.0"),sQuery(id+"F0.wireOp",EDGE,"E2.2"),sQuery(id+"F0.wireOp",EDGE,"E2.4"),sQuery(id+"F0.wireOp",EDGE,"E14.1"),sQuery(id+"F0.wireOp",EDGE,"E14.2"),sQuery(id+"F0.wireOp",EDGE,"E14.3"),sQuery(id+"F0.wireOp",EDGE,"E14.4"),sQuery(id+"F0.wireOp",EDGE,"E14.5"),sQuery(id+"F0.wireOp",EDGE,"E15.1"),sQuery(id+"F0.wireOp",EDGE,"E15.2"),sQuery(id+"F0.wireOp",EDGE,"E15.3"),sQuery(id+"F0.wireOp",EDGE,"E15.4"),sQuery(id+"F0.wireOp",EDGE,"E15.5"),sQuery(id+"F0.wireOp",EDGE,"E19.1"),sQuery(id+"F0.wireOp",EDGE,"E19.2"),sQuery(id+"F0.wireOp",EDGE,"E19.3"),sQuery(id+"F0.wireOp",EDGE,"E19.4"),subQ0])],"isStart":true})],"blendedInto":[makeQuery(id+"F1.opExtrude","CAP_FACE",FACE,{"disambiguationData":[OSD([sQuery(id+"F0.wireOp",EDGE,"E0"),sQuery(id+"F0.wireOp",EDGE,"E2.0"),sQuery(id+"F0.wireOp",EDGE,"E2.2"),sQuery(id+"F0.wireOp",EDGE,"E2.4"),sQuery(id+"F0.wireOp",EDGE,"E14.1"),sQuery(id+"F0.wireOp",EDGE,"E14.2"),sQuery(id+"F0.wireOp",EDGE,"E14.3"),sQuery(id+"F0.wireOp",EDGE,"E14.4"),sQuery(id+"F0.wireOp",EDGE,"E14.5"),sQuery(id+"F0.wireOp",EDGE,"E15.1"),sQuery(id+"F0.wireOp",EDGE,"E15.2"),sQuery(id+"F0.wireOp",EDGE,"E15.3"),sQuery(id+"F0.wireOp",EDGE,"E15.4"),sQuery(id+"F0.wireOp",EDGE,"E15.5"),sQuery(id+"F0.wireOp",EDGE,"E19.1"),sQuery(id+"F0.wireOp",EDGE,"E19.2"),sQuery(id+"F0.wireOp",EDGE,"E19.3"),sQuery(id+"F0.wireOp",EDGE,"E19.4"),subQ0])],"isStart":true})]});}
            var Q5;
            {var subQ0=sQuery(id+"F0.wireOp",EDGE,"E19.4");Q5=makeQuery(id+"F2.opChamfer","BLEND_EDGE",EDGE,{"blendedFrom":[makeQuery(id+"F1.opExtrude","CAP_EDGE",EDGE,{"disambiguationData":[OSD([subQ0])],"isStart":true}),makeQuery(id+"F1.opExtrude","CAP_FACE",FACE,{"disambiguationData":[OSD([sQuery(id+"F0.wireOp",EDGE,"E0"),sQuery(id+"F0.wireOp",EDGE,"E2.0"),sQuery(id+"F0.wireOp",EDGE,"E2.2"),sQuery(id+"F0.wireOp",EDGE,"E2.4"),sQuery(id+"F0.wireOp",EDGE,"E14.1"),sQuery(id+"F0.wireOp",EDGE,"E14.2"),sQuery(id+"F0.wireOp",EDGE,"E14.3"),sQuery(id+"F0.wireOp",EDGE,"E14.4"),sQuery(id+"F0.wireOp",EDGE,"E14.5"),sQuery(id+"F0.wireOp",EDGE,"E15.1"),sQuery(id+"F0.wireOp",EDGE,"E15.2"),sQuery(id+"F0.wireOp",EDGE,"E15.3"),sQuery(id+"F0.wireOp",EDGE,"E15.4"),sQuery(id+"F0.wireOp",EDGE,"E15.5"),sQuery(id+"F0.wireOp",EDGE,"E19.1"),sQuery(id+"F0.wireOp",EDGE,"E19.2"),sQuery(id+"F0.wireOp",EDGE,"E19.3"),subQ0,sQuery(id+"F0.wireOp",EDGE,"E19.5")])],"isStart":true})],"blendedInto":[makeQuery(id+"F1.opExtrude","CAP_FACE",FACE,{"disambiguationData":[OSD([sQuery(id+"F0.wireOp",EDGE,"E0"),sQuery(id+"F0.wireOp",EDGE,"E2.0"),sQuery(id+"F0.wireOp",EDGE,"E2.2"),sQuery(id+"F0.wireOp",EDGE,"E2.4"),sQuery(id+"F0.wireOp",EDGE,"E14.1"),sQuery(id+"F0.wireOp",EDGE,"E14.2"),sQuery(id+"F0.wireOp",EDGE,"E14.3"),sQuery(id+"F0.wireOp",EDGE,"E14.4"),sQuery(id+"F0.wireOp",EDGE,"E14.5"),sQuery(id+"F0.wireOp",EDGE,"E15.1"),sQuery(id+"F0.wireOp",EDGE,"E15.2"),sQuery(id+"F0.wireOp",EDGE,"E15.3"),sQuery(id+"F0.wireOp",EDGE,"E15.4"),sQuery(id+"F0.wireOp",EDGE,"E15.5"),sQuery(id+"F0.wireOp",EDGE,"E19.1"),sQuery(id+"F0.wireOp",EDGE,"E19.2"),sQuery(id+"F0.wireOp",EDGE,"E19.3"),subQ0,sQuery(id+"F0.wireOp",EDGE,"E19.5")])],"isStart":true})]});}
            var Q6;
            {var subQ0=sQuery(id+"F0.wireOp",EDGE,"E19.2");Q6=makeQuery(id+"F2.opChamfer","BLEND_EDGE",EDGE,{"blendedFrom":[makeQuery(id+"F1.opExtrude","CAP_EDGE",EDGE,{"disambiguationData":[OSD([subQ0])],"isStart":true}),makeQuery(id+"F1.opExtrude","CAP_FACE",FACE,{"disambiguationData":[OSD([sQuery(id+"F0.wireOp",EDGE,"E0"),sQuery(id+"F0.wireOp",EDGE,"E2.0"),sQuery(id+"F0.wireOp",EDGE,"E2.2"),sQuery(id+"F0.wireOp",EDGE,"E2.4"),sQuery(id+"F0.wireOp",EDGE,"E14.1"),sQuery(id+"F0.wireOp",EDGE,"E14.2"),sQuery(id+"F0.wireOp",EDGE,"E14.3"),sQuery(id+"F0.wireOp",EDGE,"E14.4"),sQuery(id+"F0.wireOp",EDGE,"E14.5"),sQuery(id+"F0.wireOp",EDGE,"E15.1"),sQuery(id+"F0.wireOp",EDGE,"E15.2"),sQuery(id+"F0.wireOp",EDGE,"E15.3"),sQuery(id+"F0.wireOp",EDGE,"E15.4"),sQuery(id+"F0.wireOp",EDGE,"E15.5"),sQuery(id+"F0.wireOp",EDGE,"E19.1"),subQ0,sQuery(id+"F0.wireOp",EDGE,"E19.3"),sQuery(id+"F0.wireOp",EDGE,"E19.4"),sQuery(id+"F0.wireOp",EDGE,"E19.5")])],"isStart":true})],"blendedInto":[makeQuery(id+"F1.opExtrude","CAP_FACE",FACE,{"disambiguationData":[OSD([sQuery(id+"F0.wireOp",EDGE,"E0"),sQuery(id+"F0.wireOp",EDGE,"E2.0"),sQuery(id+"F0.wireOp",EDGE,"E2.2"),sQuery(id+"F0.wireOp",EDGE,"E2.4"),sQuery(id+"F0.wireOp",EDGE,"E14.1"),sQuery(id+"F0.wireOp",EDGE,"E14.2"),sQuery(id+"F0.wireOp",EDGE,"E14.3"),sQuery(id+"F0.wireOp",EDGE,"E14.4"),sQuery(id+"F0.wireOp",EDGE,"E14.5"),sQuery(id+"F0.wireOp",EDGE,"E15.1"),sQuery(id+"F0.wireOp",EDGE,"E15.2"),sQuery(id+"F0.wireOp",EDGE,"E15.3"),sQuery(id+"F0.wireOp",EDGE,"E15.4"),sQuery(id+"F0.wireOp",EDGE,"E15.5"),sQuery(id+"F0.wireOp",EDGE,"E19.1"),subQ0,sQuery(id+"F0.wireOp",EDGE,"E19.3"),sQuery(id+"F0.wireOp",EDGE,"E19.4"),sQuery(id+"F0.wireOp",EDGE,"E19.5")])],"isStart":true})]});}
            var Q7;
            {var subQ0=sQuery(id+"F0.wireOp",EDGE,"E19.1");Q7=makeQuery(id+"F2.opChamfer","BLEND_EDGE",EDGE,{"blendedFrom":[makeQuery(id+"F1.opExtrude","CAP_EDGE",EDGE,{"disambiguationData":[OSD([subQ0])],"isStart":true}),makeQuery(id+"F1.opExtrude","CAP_FACE",FACE,{"disambiguationData":[OSD([sQuery(id+"F0.wireOp",EDGE,"E0"),sQuery(id+"F0.wireOp",EDGE,"E2.0"),sQuery(id+"F0.wireOp",EDGE,"E2.2"),sQuery(id+"F0.wireOp",EDGE,"E2.4"),sQuery(id+"F0.wireOp",EDGE,"E14.1"),sQuery(id+"F0.wireOp",EDGE,"E14.2"),sQuery(id+"F0.wireOp",EDGE,"E14.3"),sQuery(id+"F0.wireOp",EDGE,"E14.4"),sQuery(id+"F0.wireOp",EDGE,"E14.5"),sQuery(id+"F0.wireOp",EDGE,"E15.1"),sQuery(id+"F0.wireOp",EDGE,"E15.2"),sQuery(id+"F0.wireOp",EDGE,"E15.3"),sQuery(id+"F0.wireOp",EDGE,"E15.4"),sQuery(id+"F0.wireOp",EDGE,"E15.5"),subQ0,sQuery(id+"F0.wireOp",EDGE,"E19.2"),sQuery(id+"F0.wireOp",EDGE,"E19.3"),sQuery(id+"F0.wireOp",EDGE,"E19.4"),sQuery(id+"F0.wireOp",EDGE,"E19.5")])],"isStart":true})],"blendedInto":[makeQuery(id+"F1.opExtrude","CAP_FACE",FACE,{"disambiguationData":[OSD([sQuery(id+"F0.wireOp",EDGE,"E0"),sQuery(id+"F0.wireOp",EDGE,"E2.0"),sQuery(id+"F0.wireOp",EDGE,"E2.2"),sQuery(id+"F0.wireOp",EDGE,"E2.4"),sQuery(id+"F0.wireOp",EDGE,"E14.1"),sQuery(id+"F0.wireOp",EDGE,"E14.2"),sQuery(id+"F0.wireOp",EDGE,"E14.3"),sQuery(id+"F0.wireOp",EDGE,"E14.4"),sQuery(id+"F0.wireOp",EDGE,"E14.5"),sQuery(id+"F0.wireOp",EDGE,"E15.1"),sQuery(id+"F0.wireOp",EDGE,"E15.2"),sQuery(id+"F0.wireOp",EDGE,"E15.3"),sQuery(id+"F0.wireOp",EDGE,"E15.4"),sQuery(id+"F0.wireOp",EDGE,"E15.5"),subQ0,sQuery(id+"F0.wireOp",EDGE,"E19.2"),sQuery(id+"F0.wireOp",EDGE,"E19.3"),sQuery(id+"F0.wireOp",EDGE,"E19.4"),sQuery(id+"F0.wireOp",EDGE,"E19.5")])],"isStart":true})]});}
            var Q8;
            {var subQ0=sQuery(id+"F0.wireOp",EDGE,"E14.5");Q8=makeQuery(id+"F2.opChamfer","BLEND_EDGE",EDGE,{"blendedFrom":[makeQuery(id+"F1.opExtrude","CAP_EDGE",EDGE,{"disambiguationData":[OSD([subQ0])],"isStart":true}),makeQuery(id+"F1.opExtrude","CAP_FACE",FACE,{"disambiguationData":[OSD([sQuery(id+"F0.wireOp",EDGE,"E0"),sQuery(id+"F0.wireOp",EDGE,"E2.0"),sQuery(id+"F0.wireOp",EDGE,"E2.2"),sQuery(id+"F0.wireOp",EDGE,"E2.4"),sQuery(id+"F0.wireOp",EDGE,"E14.1"),sQuery(id+"F0.wireOp",EDGE,"E14.2"),sQuery(id+"F0.wireOp",EDGE,"E14.3"),sQuery(id+"F0.wireOp",EDGE,"E14.4"),subQ0,sQuery(id+"F0.wireOp",EDGE,"E15.1"),sQuery(id+"F0.wireOp",EDGE,"E15.2"),sQuery(id+"F0.wireOp",EDGE,"E15.3"),sQuery(id+"F0.wireOp",EDGE,"E15.4"),sQuery(id+"F0.wireOp",EDGE,"E15.5"),sQuery(id+"F0.wireOp",EDGE,"E19.1"),sQuery(id+"F0.wireOp",EDGE,"E19.2"),sQuery(id+"F0.wireOp",EDGE,"E19.3"),sQuery(id+"F0.wireOp",EDGE,"E19.4"),sQuery(id+"F0.wireOp",EDGE,"E19.5")])],"isStart":true})],"blendedInto":[makeQuery(id+"F1.opExtrude","CAP_FACE",FACE,{"disambiguationData":[OSD([sQuery(id+"F0.wireOp",EDGE,"E0"),sQuery(id+"F0.wireOp",EDGE,"E2.0"),sQuery(id+"F0.wireOp",EDGE,"E2.2"),sQuery(id+"F0.wireOp",EDGE,"E2.4"),sQuery(id+"F0.wireOp",EDGE,"E14.1"),sQuery(id+"F0.wireOp",EDGE,"E14.2"),sQuery(id+"F0.wireOp",EDGE,"E14.3"),sQuery(id+"F0.wireOp",EDGE,"E14.4"),subQ0,sQuery(id+"F0.wireOp",EDGE,"E15.1"),sQuery(id+"F0.wireOp",EDGE,"E15.2"),sQuery(id+"F0.wireOp",EDGE,"E15.3"),sQuery(id+"F0.wireOp",EDGE,"E15.4"),sQuery(id+"F0.wireOp",EDGE,"E15.5"),sQuery(id+"F0.wireOp",EDGE,"E19.1"),sQuery(id+"F0.wireOp",EDGE,"E19.2"),sQuery(id+"F0.wireOp",EDGE,"E19.3"),sQuery(id+"F0.wireOp",EDGE,"E19.4"),sQuery(id+"F0.wireOp",EDGE,"E19.5")])],"isStart":true})]});}
            var Q9;
            {var subQ0=sQuery(id+"F0.wireOp",EDGE,"E14.4");Q9=makeQuery(id+"F2.opChamfer","BLEND_EDGE",EDGE,{"blendedFrom":[makeQuery(id+"F1.opExtrude","CAP_EDGE",EDGE,{"disambiguationData":[OSD([subQ0])],"isStart":true}),makeQuery(id+"F1.opExtrude","CAP_FACE",FACE,{"disambiguationData":[OSD([sQuery(id+"F0.wireOp",EDGE,"E0"),sQuery(id+"F0.wireOp",EDGE,"E2.0"),sQuery(id+"F0.wireOp",EDGE,"E2.2"),sQuery(id+"F0.wireOp",EDGE,"E2.4"),sQuery(id+"F0.wireOp",EDGE,"E14.1"),sQuery(id+"F0.wireOp",EDGE,"E14.2"),sQuery(id+"F0.wireOp",EDGE,"E14.3"),subQ0,sQuery(id+"F0.wireOp",EDGE,"E14.5"),sQuery(id+"F0.wireOp",EDGE,"E15.1"),sQuery(id+"F0.wireOp",EDGE,"E15.2"),sQuery(id+"F0.wireOp",EDGE,"E15.3"),sQuery(id+"F0.wireOp",EDGE,"E15.4"),sQuery(id+"F0.wireOp",EDGE,"E15.5"),sQuery(id+"F0.wireOp",EDGE,"E19.1"),sQuery(id+"F0.wireOp",EDGE,"E19.2"),sQuery(id+"F0.wireOp",EDGE,"E19.3"),sQuery(id+"F0.wireOp",EDGE,"E19.4"),sQuery(id+"F0.wireOp",EDGE,"E19.5")])],"isStart":true})],"blendedInto":[makeQuery(id+"F1.opExtrude","CAP_FACE",FACE,{"disambiguationData":[OSD([sQuery(id+"F0.wireOp",EDGE,"E0"),sQuery(id+"F0.wireOp",EDGE,"E2.0"),sQuery(id+"F0.wireOp",EDGE,"E2.2"),sQuery(id+"F0.wireOp",EDGE,"E2.4"),sQuery(id+"F0.wireOp",EDGE,"E14.1"),sQuery(id+"F0.wireOp",EDGE,"E14.2"),sQuery(id+"F0.wireOp",EDGE,"E14.3"),subQ0,sQuery(id+"F0.wireOp",EDGE,"E14.5"),sQuery(id+"F0.wireOp",EDGE,"E15.1"),sQuery(id+"F0.wireOp",EDGE,"E15.2"),sQuery(id+"F0.wireOp",EDGE,"E15.3"),sQuery(id+"F0.wireOp",EDGE,"E15.4"),sQuery(id+"F0.wireOp",EDGE,"E15.5"),sQuery(id+"F0.wireOp",EDGE,"E19.1"),sQuery(id+"F0.wireOp",EDGE,"E19.2"),sQuery(id+"F0.wireOp",EDGE,"E19.3"),sQuery(id+"F0.wireOp",EDGE,"E19.4"),sQuery(id+"F0.wireOp",EDGE,"E19.5")])],"isStart":true})]});}
            var Q10;
            {var subQ0=sQuery(id+"F0.wireOp",EDGE,"E14.2");Q10=makeQuery(id+"F2.opChamfer","BLEND_EDGE",EDGE,{"blendedFrom":[makeQuery(id+"F1.opExtrude","CAP_EDGE",EDGE,{"disambiguationData":[OSD([subQ0])],"isStart":true}),makeQuery(id+"F1.opExtrude","CAP_FACE",FACE,{"disambiguationData":[OSD([sQuery(id+"F0.wireOp",EDGE,"E0"),sQuery(id+"F0.wireOp",EDGE,"E2.0"),sQuery(id+"F0.wireOp",EDGE,"E2.2"),sQuery(id+"F0.wireOp",EDGE,"E2.4"),sQuery(id+"F0.wireOp",EDGE,"E14.1"),subQ0,sQuery(id+"F0.wireOp",EDGE,"E14.3"),sQuery(id+"F0.wireOp",EDGE,"E14.4"),sQuery(id+"F0.wireOp",EDGE,"E14.5"),sQuery(id+"F0.wireOp",EDGE,"E15.1"),sQuery(id+"F0.wireOp",EDGE,"E15.2"),sQuery(id+"F0.wireOp",EDGE,"E15.3"),sQuery(id+"F0.wireOp",EDGE,"E15.4"),sQuery(id+"F0.wireOp",EDGE,"E15.5"),sQuery(id+"F0.wireOp",EDGE,"E19.1"),sQuery(id+"F0.wireOp",EDGE,"E19.2"),sQuery(id+"F0.wireOp",EDGE,"E19.3"),sQuery(id+"F0.wireOp",EDGE,"E19.4"),sQuery(id+"F0.wireOp",EDGE,"E19.5")])],"isStart":true})],"blendedInto":[makeQuery(id+"F1.opExtrude","CAP_FACE",FACE,{"disambiguationData":[OSD([sQuery(id+"F0.wireOp",EDGE,"E0"),sQuery(id+"F0.wireOp",EDGE,"E2.0"),sQuery(id+"F0.wireOp",EDGE,"E2.2"),sQuery(id+"F0.wireOp",EDGE,"E2.4"),sQuery(id+"F0.wireOp",EDGE,"E14.1"),subQ0,sQuery(id+"F0.wireOp",EDGE,"E14.3"),sQuery(id+"F0.wireOp",EDGE,"E14.4"),sQuery(id+"F0.wireOp",EDGE,"E14.5"),sQuery(id+"F0.wireOp",EDGE,"E15.1"),sQuery(id+"F0.wireOp",EDGE,"E15.2"),sQuery(id+"F0.wireOp",EDGE,"E15.3"),sQuery(id+"F0.wireOp",EDGE,"E15.4"),sQuery(id+"F0.wireOp",EDGE,"E15.5"),sQuery(id+"F0.wireOp",EDGE,"E19.1"),sQuery(id+"F0.wireOp",EDGE,"E19.2"),sQuery(id+"F0.wireOp",EDGE,"E19.3"),sQuery(id+"F0.wireOp",EDGE,"E19.4"),sQuery(id+"F0.wireOp",EDGE,"E19.5")])],"isStart":true})]});}
            var Q11;
            {var subQ0=sQuery(id+"F0.wireOp",EDGE,"E14.1");Q11=makeQuery(id+"F2.opChamfer","BLEND_EDGE",EDGE,{"blendedFrom":[makeQuery(id+"F1.opExtrude","CAP_EDGE",EDGE,{"disambiguationData":[OSD([subQ0])],"isStart":true}),makeQuery(id+"F1.opExtrude","CAP_FACE",FACE,{"disambiguationData":[OSD([sQuery(id+"F0.wireOp",EDGE,"E0"),sQuery(id+"F0.wireOp",EDGE,"E2.0"),sQuery(id+"F0.wireOp",EDGE,"E2.2"),sQuery(id+"F0.wireOp",EDGE,"E2.4"),subQ0,sQuery(id+"F0.wireOp",EDGE,"E14.2"),sQuery(id+"F0.wireOp",EDGE,"E14.3"),sQuery(id+"F0.wireOp",EDGE,"E14.4"),sQuery(id+"F0.wireOp",EDGE,"E14.5"),sQuery(id+"F0.wireOp",EDGE,"E15.1"),sQuery(id+"F0.wireOp",EDGE,"E15.2"),sQuery(id+"F0.wireOp",EDGE,"E15.3"),sQuery(id+"F0.wireOp",EDGE,"E15.4"),sQuery(id+"F0.wireOp",EDGE,"E15.5"),sQuery(id+"F0.wireOp",EDGE,"E19.1"),sQuery(id+"F0.wireOp",EDGE,"E19.2"),sQuery(id+"F0.wireOp",EDGE,"E19.3"),sQuery(id+"F0.wireOp",EDGE,"E19.4"),sQuery(id+"F0.wireOp",EDGE,"E19.5")])],"isStart":true})],"blendedInto":[makeQuery(id+"F1.opExtrude","CAP_FACE",FACE,{"disambiguationData":[OSD([sQuery(id+"F0.wireOp",EDGE,"E0"),sQuery(id+"F0.wireOp",EDGE,"E2.0"),sQuery(id+"F0.wireOp",EDGE,"E2.2"),sQuery(id+"F0.wireOp",EDGE,"E2.4"),subQ0,sQuery(id+"F0.wireOp",EDGE,"E14.2"),sQuery(id+"F0.wireOp",EDGE,"E14.3"),sQuery(id+"F0.wireOp",EDGE,"E14.4"),sQuery(id+"F0.wireOp",EDGE,"E14.5"),sQuery(id+"F0.wireOp",EDGE,"E15.1"),sQuery(id+"F0.wireOp",EDGE,"E15.2"),sQuery(id+"F0.wireOp",EDGE,"E15.3"),sQuery(id+"F0.wireOp",EDGE,"E15.4"),sQuery(id+"F0.wireOp",EDGE,"E15.5"),sQuery(id+"F0.wireOp",EDGE,"E19.1"),sQuery(id+"F0.wireOp",EDGE,"E19.2"),sQuery(id+"F0.wireOp",EDGE,"E19.3"),sQuery(id+"F0.wireOp",EDGE,"E19.4"),sQuery(id+"F0.wireOp",EDGE,"E19.5")])],"isStart":true})]});}
            chamfer(context, id + "F7", {"entities" : qUnion([Q0, Q1, Q2, Q3, Q4, Q5, Q6, Q7, Q8, Q9, Q10, Q11]), "width" : 3 * mm, "tangentPropagation" : true});
        }
        {
            var Q0;
            {var subQ0=sQuery(id+"F0.wireOp",EDGE,"E15.4");var subQ1=makeQuery(id+"F1.opExtrude","CAP_FACE",FACE,{"disambiguationData":[OSD([sQuery(id+"F0.wireOp",EDGE,"E0"),sQuery(id+"F0.wireOp",EDGE,"E2.0"),sQuery(id+"F0.wireOp",EDGE,"E2.2"),sQuery(id+"F0.wireOp",EDGE,"E2.4"),sQuery(id+"F0.wireOp",EDGE,"E14.1"),sQuery(id+"F0.wireOp",EDGE,"E14.2"),sQuery(id+"F0.wireOp",EDGE,"E14.3"),sQuery(id+"F0.wireOp",EDGE,"E14.4"),sQuery(id+"F0.wireOp",EDGE,"E14.5"),sQuery(id+"F0.wireOp",EDGE,"E15.1"),sQuery(id+"F0.wireOp",EDGE,"E15.2"),sQuery(id+"F0.wireOp",EDGE,"E15.3"),subQ0,sQuery(id+"F0.wireOp",EDGE,"E15.5"),sQuery(id+"F0.wireOp",EDGE,"E19.1"),sQuery(id+"F0.wireOp",EDGE,"E19.2"),sQuery(id+"F0.wireOp",EDGE,"E19.3"),sQuery(id+"F0.wireOp",EDGE,"E19.4"),sQuery(id+"F0.wireOp",EDGE,"E19.5")])],"isStart":true});Q0=makeQuery(id+"F7.opChamfer","BLEND_EDGE",EDGE,{"blendedFrom":[makeQuery(id+"F2.opChamfer","BLEND_EDGE",EDGE,{"blendedFrom":[makeQuery(id+"F1.opExtrude","CAP_EDGE",EDGE,{"disambiguationData":[OSD([subQ0])],"isStart":true}),subQ1],"blendedInto":[subQ1]}),subQ1],"blendedInto":[subQ1]});}
            var Q1;
            {var subQ0=sQuery(id+"F0.wireOp",EDGE,"E15.5");var subQ1=makeQuery(id+"F1.opExtrude","CAP_FACE",FACE,{"disambiguationData":[OSD([sQuery(id+"F0.wireOp",EDGE,"E0"),sQuery(id+"F0.wireOp",EDGE,"E2.0"),sQuery(id+"F0.wireOp",EDGE,"E2.2"),sQuery(id+"F0.wireOp",EDGE,"E2.4"),sQuery(id+"F0.wireOp",EDGE,"E14.1"),sQuery(id+"F0.wireOp",EDGE,"E14.2"),sQuery(id+"F0.wireOp",EDGE,"E14.3"),sQuery(id+"F0.wireOp",EDGE,"E14.4"),sQuery(id+"F0.wireOp",EDGE,"E14.5"),sQuery(id+"F0.wireOp",EDGE,"E15.1"),sQuery(id+"F0.wireOp",EDGE,"E15.2"),sQuery(id+"F0.wireOp",EDGE,"E15.3"),sQuery(id+"F0.wireOp",EDGE,"E15.4"),subQ0,sQuery(id+"F0.wireOp",EDGE,"E19.1"),sQuery(id+"F0.wireOp",EDGE,"E19.2"),sQuery(id+"F0.wireOp",EDGE,"E19.3"),sQuery(id+"F0.wireOp",EDGE,"E19.4"),sQuery(id+"F0.wireOp",EDGE,"E19.5")])],"isStart":true});Q1=makeQuery(id+"F7.opChamfer","BLEND_EDGE",EDGE,{"blendedFrom":[makeQuery(id+"F2.opChamfer","BLEND_EDGE",EDGE,{"blendedFrom":[makeQuery(id+"F1.opExtrude","CAP_EDGE",EDGE,{"disambiguationData":[OSD([subQ0])],"isStart":true}),subQ1],"blendedInto":[subQ1]}),subQ1],"blendedInto":[subQ1]});}
            var Q2;
            {var subQ0=sQuery(id+"F0.wireOp",EDGE,"E15.2");var subQ1=makeQuery(id+"F1.opExtrude","CAP_FACE",FACE,{"disambiguationData":[OSD([sQuery(id+"F0.wireOp",EDGE,"E0"),sQuery(id+"F0.wireOp",EDGE,"E2.0"),sQuery(id+"F0.wireOp",EDGE,"E2.2"),sQuery(id+"F0.wireOp",EDGE,"E2.4"),sQuery(id+"F0.wireOp",EDGE,"E14.1"),sQuery(id+"F0.wireOp",EDGE,"E14.2"),sQuery(id+"F0.wireOp",EDGE,"E14.3"),sQuery(id+"F0.wireOp",EDGE,"E14.4"),sQuery(id+"F0.wireOp",EDGE,"E14.5"),sQuery(id+"F0.wireOp",EDGE,"E15.1"),subQ0,sQuery(id+"F0.wireOp",EDGE,"E15.3"),sQuery(id+"F0.wireOp",EDGE,"E15.4"),sQuery(id+"F0.wireOp",EDGE,"E15.5"),sQuery(id+"F0.wireOp",EDGE,"E19.1"),sQuery(id+"F0.wireOp",EDGE,"E19.2"),sQuery(id+"F0.wireOp",EDGE,"E19.3"),sQuery(id+"F0.wireOp",EDGE,"E19.4"),sQuery(id+"F0.wireOp",EDGE,"E19.5")])],"isStart":true});Q2=makeQuery(id+"F7.opChamfer","BLEND_EDGE",EDGE,{"blendedFrom":[makeQuery(id+"F2.opChamfer","BLEND_EDGE",EDGE,{"blendedFrom":[makeQuery(id+"F1.opExtrude","CAP_EDGE",EDGE,{"disambiguationData":[OSD([subQ0])],"isStart":true}),subQ1],"blendedInto":[subQ1]}),subQ1],"blendedInto":[subQ1]});}
            var Q3;
            {var subQ0=sQuery(id+"F0.wireOp",EDGE,"E15.1");var subQ1=makeQuery(id+"F1.opExtrude","CAP_FACE",FACE,{"disambiguationData":[OSD([sQuery(id+"F0.wireOp",EDGE,"E0"),sQuery(id+"F0.wireOp",EDGE,"E2.0"),sQuery(id+"F0.wireOp",EDGE,"E2.2"),sQuery(id+"F0.wireOp",EDGE,"E2.4"),sQuery(id+"F0.wireOp",EDGE,"E14.1"),sQuery(id+"F0.wireOp",EDGE,"E14.2"),sQuery(id+"F0.wireOp",EDGE,"E14.3"),sQuery(id+"F0.wireOp",EDGE,"E14.4"),sQuery(id+"F0.wireOp",EDGE,"E14.5"),subQ0,sQuery(id+"F0.wireOp",EDGE,"E15.2"),sQuery(id+"F0.wireOp",EDGE,"E15.3"),sQuery(id+"F0.wireOp",EDGE,"E15.4"),sQuery(id+"F0.wireOp",EDGE,"E15.5"),sQuery(id+"F0.wireOp",EDGE,"E19.1"),sQuery(id+"F0.wireOp",EDGE,"E19.2"),sQuery(id+"F0.wireOp",EDGE,"E19.3"),sQuery(id+"F0.wireOp",EDGE,"E19.4"),sQuery(id+"F0.wireOp",EDGE,"E19.5")])],"isStart":true});Q3=makeQuery(id+"F7.opChamfer","BLEND_EDGE",EDGE,{"blendedFrom":[makeQuery(id+"F2.opChamfer","BLEND_EDGE",EDGE,{"blendedFrom":[makeQuery(id+"F1.opExtrude","CAP_EDGE",EDGE,{"disambiguationData":[OSD([subQ0])],"isStart":true}),subQ1],"blendedInto":[subQ1]}),subQ1],"blendedInto":[subQ1]});}
            var Q4;
            {var subQ0=sQuery(id+"F0.wireOp",EDGE,"E14.1");var subQ1=makeQuery(id+"F1.opExtrude","CAP_FACE",FACE,{"disambiguationData":[OSD([sQuery(id+"F0.wireOp",EDGE,"E0"),sQuery(id+"F0.wireOp",EDGE,"E2.0"),sQuery(id+"F0.wireOp",EDGE,"E2.2"),sQuery(id+"F0.wireOp",EDGE,"E2.4"),subQ0,sQuery(id+"F0.wireOp",EDGE,"E14.2"),sQuery(id+"F0.wireOp",EDGE,"E14.3"),sQuery(id+"F0.wireOp",EDGE,"E14.4"),sQuery(id+"F0.wireOp",EDGE,"E14.5"),sQuery(id+"F0.wireOp",EDGE,"E15.1"),sQuery(id+"F0.wireOp",EDGE,"E15.2"),sQuery(id+"F0.wireOp",EDGE,"E15.3"),sQuery(id+"F0.wireOp",EDGE,"E15.4"),sQuery(id+"F0.wireOp",EDGE,"E15.5"),sQuery(id+"F0.wireOp",EDGE,"E19.1"),sQuery(id+"F0.wireOp",EDGE,"E19.2"),sQuery(id+"F0.wireOp",EDGE,"E19.3"),sQuery(id+"F0.wireOp",EDGE,"E19.4"),sQuery(id+"F0.wireOp",EDGE,"E19.5")])],"isStart":true});Q4=makeQuery(id+"F7.opChamfer","BLEND_EDGE",EDGE,{"blendedFrom":[makeQuery(id+"F2.opChamfer","BLEND_EDGE",EDGE,{"blendedFrom":[makeQuery(id+"F1.opExtrude","CAP_EDGE",EDGE,{"disambiguationData":[OSD([subQ0])],"isStart":true}),subQ1],"blendedInto":[subQ1]}),subQ1],"blendedInto":[subQ1]});}
            var Q5;
            {var subQ0=sQuery(id+"F0.wireOp",EDGE,"E14.2");var subQ1=makeQuery(id+"F1.opExtrude","CAP_FACE",FACE,{"disambiguationData":[OSD([sQuery(id+"F0.wireOp",EDGE,"E0"),sQuery(id+"F0.wireOp",EDGE,"E2.0"),sQuery(id+"F0.wireOp",EDGE,"E2.2"),sQuery(id+"F0.wireOp",EDGE,"E2.4"),sQuery(id+"F0.wireOp",EDGE,"E14.1"),subQ0,sQuery(id+"F0.wireOp",EDGE,"E14.3"),sQuery(id+"F0.wireOp",EDGE,"E14.4"),sQuery(id+"F0.wireOp",EDGE,"E14.5"),sQuery(id+"F0.wireOp",EDGE,"E15.1"),sQuery(id+"F0.wireOp",EDGE,"E15.2"),sQuery(id+"F0.wireOp",EDGE,"E15.3"),sQuery(id+"F0.wireOp",EDGE,"E15.4"),sQuery(id+"F0.wireOp",EDGE,"E15.5"),sQuery(id+"F0.wireOp",EDGE,"E19.1"),sQuery(id+"F0.wireOp",EDGE,"E19.2"),sQuery(id+"F0.wireOp",EDGE,"E19.3"),sQuery(id+"F0.wireOp",EDGE,"E19.4"),sQuery(id+"F0.wireOp",EDGE,"E19.5")])],"isStart":true});Q5=makeQuery(id+"F7.opChamfer","BLEND_EDGE",EDGE,{"blendedFrom":[makeQuery(id+"F2.opChamfer","BLEND_EDGE",EDGE,{"blendedFrom":[makeQuery(id+"F1.opExtrude","CAP_EDGE",EDGE,{"disambiguationData":[OSD([subQ0])],"isStart":true}),subQ1],"blendedInto":[subQ1]}),subQ1],"blendedInto":[subQ1]});}
            var Q6;
            {var subQ0=sQuery(id+"F0.wireOp",EDGE,"E14.4");var subQ1=makeQuery(id+"F1.opExtrude","CAP_FACE",FACE,{"disambiguationData":[OSD([sQuery(id+"F0.wireOp",EDGE,"E0"),sQuery(id+"F0.wireOp",EDGE,"E2.0"),sQuery(id+"F0.wireOp",EDGE,"E2.2"),sQuery(id+"F0.wireOp",EDGE,"E2.4"),sQuery(id+"F0.wireOp",EDGE,"E14.1"),sQuery(id+"F0.wireOp",EDGE,"E14.2"),sQuery(id+"F0.wireOp",EDGE,"E14.3"),subQ0,sQuery(id+"F0.wireOp",EDGE,"E14.5"),sQuery(id+"F0.wireOp",EDGE,"E15.1"),sQuery(id+"F0.wireOp",EDGE,"E15.2"),sQuery(id+"F0.wireOp",EDGE,"E15.3"),sQuery(id+"F0.wireOp",EDGE,"E15.4"),sQuery(id+"F0.wireOp",EDGE,"E15.5"),sQuery(id+"F0.wireOp",EDGE,"E19.1"),sQuery(id+"F0.wireOp",EDGE,"E19.2"),sQuery(id+"F0.wireOp",EDGE,"E19.3"),sQuery(id+"F0.wireOp",EDGE,"E19.4"),sQuery(id+"F0.wireOp",EDGE,"E19.5")])],"isStart":true});Q6=makeQuery(id+"F7.opChamfer","BLEND_EDGE",EDGE,{"blendedFrom":[makeQuery(id+"F2.opChamfer","BLEND_EDGE",EDGE,{"blendedFrom":[makeQuery(id+"F1.opExtrude","CAP_EDGE",EDGE,{"disambiguationData":[OSD([subQ0])],"isStart":true}),subQ1],"blendedInto":[subQ1]}),subQ1],"blendedInto":[subQ1]});}
            var Q7;
            {var subQ0=sQuery(id+"F0.wireOp",EDGE,"E14.5");var subQ1=makeQuery(id+"F1.opExtrude","CAP_FACE",FACE,{"disambiguationData":[OSD([sQuery(id+"F0.wireOp",EDGE,"E0"),sQuery(id+"F0.wireOp",EDGE,"E2.0"),sQuery(id+"F0.wireOp",EDGE,"E2.2"),sQuery(id+"F0.wireOp",EDGE,"E2.4"),sQuery(id+"F0.wireOp",EDGE,"E14.1"),sQuery(id+"F0.wireOp",EDGE,"E14.2"),sQuery(id+"F0.wireOp",EDGE,"E14.3"),sQuery(id+"F0.wireOp",EDGE,"E14.4"),subQ0,sQuery(id+"F0.wireOp",EDGE,"E15.1"),sQuery(id+"F0.wireOp",EDGE,"E15.2"),sQuery(id+"F0.wireOp",EDGE,"E15.3"),sQuery(id+"F0.wireOp",EDGE,"E15.4"),sQuery(id+"F0.wireOp",EDGE,"E15.5"),sQuery(id+"F0.wireOp",EDGE,"E19.1"),sQuery(id+"F0.wireOp",EDGE,"E19.2"),sQuery(id+"F0.wireOp",EDGE,"E19.3"),sQuery(id+"F0.wireOp",EDGE,"E19.4"),sQuery(id+"F0.wireOp",EDGE,"E19.5")])],"isStart":true});Q7=makeQuery(id+"F7.opChamfer","BLEND_EDGE",EDGE,{"blendedFrom":[makeQuery(id+"F2.opChamfer","BLEND_EDGE",EDGE,{"blendedFrom":[makeQuery(id+"F1.opExtrude","CAP_EDGE",EDGE,{"disambiguationData":[OSD([subQ0])],"isStart":true}),subQ1],"blendedInto":[subQ1]}),subQ1],"blendedInto":[subQ1]});}
            var Q8;
            {var subQ0=sQuery(id+"F0.wireOp",EDGE,"E19.1");var subQ1=makeQuery(id+"F1.opExtrude","CAP_FACE",FACE,{"disambiguationData":[OSD([sQuery(id+"F0.wireOp",EDGE,"E0"),sQuery(id+"F0.wireOp",EDGE,"E2.0"),sQuery(id+"F0.wireOp",EDGE,"E2.2"),sQuery(id+"F0.wireOp",EDGE,"E2.4"),sQuery(id+"F0.wireOp",EDGE,"E14.1"),sQuery(id+"F0.wireOp",EDGE,"E14.2"),sQuery(id+"F0.wireOp",EDGE,"E14.3"),sQuery(id+"F0.wireOp",EDGE,"E14.4"),sQuery(id+"F0.wireOp",EDGE,"E14.5"),sQuery(id+"F0.wireOp",EDGE,"E15.1"),sQuery(id+"F0.wireOp",EDGE,"E15.2"),sQuery(id+"F0.wireOp",EDGE,"E15.3"),sQuery(id+"F0.wireOp",EDGE,"E15.4"),sQuery(id+"F0.wireOp",EDGE,"E15.5"),subQ0,sQuery(id+"F0.wireOp",EDGE,"E19.2"),sQuery(id+"F0.wireOp",EDGE,"E19.3"),sQuery(id+"F0.wireOp",EDGE,"E19.4"),sQuery(id+"F0.wireOp",EDGE,"E19.5")])],"isStart":true});Q8=makeQuery(id+"F7.opChamfer","BLEND_EDGE",EDGE,{"blendedFrom":[makeQuery(id+"F2.opChamfer","BLEND_EDGE",EDGE,{"blendedFrom":[makeQuery(id+"F1.opExtrude","CAP_EDGE",EDGE,{"disambiguationData":[OSD([subQ0])],"isStart":true}),subQ1],"blendedInto":[subQ1]}),subQ1],"blendedInto":[subQ1]});}
            var Q9;
            {var subQ0=sQuery(id+"F0.wireOp",EDGE,"E19.2");var subQ1=makeQuery(id+"F1.opExtrude","CAP_FACE",FACE,{"disambiguationData":[OSD([sQuery(id+"F0.wireOp",EDGE,"E0"),sQuery(id+"F0.wireOp",EDGE,"E2.0"),sQuery(id+"F0.wireOp",EDGE,"E2.2"),sQuery(id+"F0.wireOp",EDGE,"E2.4"),sQuery(id+"F0.wireOp",EDGE,"E14.1"),sQuery(id+"F0.wireOp",EDGE,"E14.2"),sQuery(id+"F0.wireOp",EDGE,"E14.3"),sQuery(id+"F0.wireOp",EDGE,"E14.4"),sQuery(id+"F0.wireOp",EDGE,"E14.5"),sQuery(id+"F0.wireOp",EDGE,"E15.1"),sQuery(id+"F0.wireOp",EDGE,"E15.2"),sQuery(id+"F0.wireOp",EDGE,"E15.3"),sQuery(id+"F0.wireOp",EDGE,"E15.4"),sQuery(id+"F0.wireOp",EDGE,"E15.5"),sQuery(id+"F0.wireOp",EDGE,"E19.1"),subQ0,sQuery(id+"F0.wireOp",EDGE,"E19.3"),sQuery(id+"F0.wireOp",EDGE,"E19.4"),sQuery(id+"F0.wireOp",EDGE,"E19.5")])],"isStart":true});Q9=makeQuery(id+"F7.opChamfer","BLEND_EDGE",EDGE,{"blendedFrom":[makeQuery(id+"F2.opChamfer","BLEND_EDGE",EDGE,{"blendedFrom":[makeQuery(id+"F1.opExtrude","CAP_EDGE",EDGE,{"disambiguationData":[OSD([subQ0])],"isStart":true}),subQ1],"blendedInto":[subQ1]}),subQ1],"blendedInto":[subQ1]});}
            var Q10;
            {var subQ0=sQuery(id+"F0.wireOp",EDGE,"E19.5");var subQ1=makeQuery(id+"F1.opExtrude","CAP_FACE",FACE,{"disambiguationData":[OSD([sQuery(id+"F0.wireOp",EDGE,"E0"),sQuery(id+"F0.wireOp",EDGE,"E2.0"),sQuery(id+"F0.wireOp",EDGE,"E2.2"),sQuery(id+"F0.wireOp",EDGE,"E2.4"),sQuery(id+"F0.wireOp",EDGE,"E14.1"),sQuery(id+"F0.wireOp",EDGE,"E14.2"),sQuery(id+"F0.wireOp",EDGE,"E14.3"),sQuery(id+"F0.wireOp",EDGE,"E14.4"),sQuery(id+"F0.wireOp",EDGE,"E14.5"),sQuery(id+"F0.wireOp",EDGE,"E15.1"),sQuery(id+"F0.wireOp",EDGE,"E15.2"),sQuery(id+"F0.wireOp",EDGE,"E15.3"),sQuery(id+"F0.wireOp",EDGE,"E15.4"),sQuery(id+"F0.wireOp",EDGE,"E15.5"),sQuery(id+"F0.wireOp",EDGE,"E19.1"),sQuery(id+"F0.wireOp",EDGE,"E19.2"),sQuery(id+"F0.wireOp",EDGE,"E19.3"),sQuery(id+"F0.wireOp",EDGE,"E19.4"),subQ0])],"isStart":true});Q10=makeQuery(id+"F7.opChamfer","BLEND_EDGE",EDGE,{"blendedFrom":[makeQuery(id+"F2.opChamfer","BLEND_EDGE",EDGE,{"blendedFrom":[makeQuery(id+"F1.opExtrude","CAP_EDGE",EDGE,{"disambiguationData":[OSD([subQ0])],"isStart":true}),subQ1],"blendedInto":[subQ1]}),subQ1],"blendedInto":[subQ1]});}
            var Q11;
            {var subQ0=sQuery(id+"F0.wireOp",EDGE,"E19.4");var subQ1=makeQuery(id+"F1.opExtrude","CAP_FACE",FACE,{"disambiguationData":[OSD([sQuery(id+"F0.wireOp",EDGE,"E0"),sQuery(id+"F0.wireOp",EDGE,"E2.0"),sQuery(id+"F0.wireOp",EDGE,"E2.2"),sQuery(id+"F0.wireOp",EDGE,"E2.4"),sQuery(id+"F0.wireOp",EDGE,"E14.1"),sQuery(id+"F0.wireOp",EDGE,"E14.2"),sQuery(id+"F0.wireOp",EDGE,"E14.3"),sQuery(id+"F0.wireOp",EDGE,"E14.4"),sQuery(id+"F0.wireOp",EDGE,"E14.5"),sQuery(id+"F0.wireOp",EDGE,"E15.1"),sQuery(id+"F0.wireOp",EDGE,"E15.2"),sQuery(id+"F0.wireOp",EDGE,"E15.3"),sQuery(id+"F0.wireOp",EDGE,"E15.4"),sQuery(id+"F0.wireOp",EDGE,"E15.5"),sQuery(id+"F0.wireOp",EDGE,"E19.1"),sQuery(id+"F0.wireOp",EDGE,"E19.2"),sQuery(id+"F0.wireOp",EDGE,"E19.3"),subQ0,sQuery(id+"F0.wireOp",EDGE,"E19.5")])],"isStart":true});Q11=makeQuery(id+"F7.opChamfer","BLEND_EDGE",EDGE,{"blendedFrom":[makeQuery(id+"F2.opChamfer","BLEND_EDGE",EDGE,{"blendedFrom":[makeQuery(id+"F1.opExtrude","CAP_EDGE",EDGE,{"disambiguationData":[OSD([subQ0])],"isStart":true}),subQ1],"blendedInto":[subQ1]}),subQ1],"blendedInto":[subQ1]});}
            chamfer(context, id + "F8", {"entities" : qUnion([Q0, Q1, Q2, Q3, Q4, Q5, Q6, Q7, Q8, Q9, Q10, Q11]), "width" : 2.5 * mm, "tangentPropagation" : true});
        }
        {
            var Q0;
            Q0=makeQuery(id+"F1.opExtrude","CAP_FACE",FACE,{"disambiguationData":[OSD([sQuery(id+"F0.wireOp",EDGE,"E0"),sQuery(id+"F0.wireOp",EDGE,"E2.0"),sQuery(id+"F0.wireOp",EDGE,"E2.2"),sQuery(id+"F0.wireOp",EDGE,"E2.4"),sQuery(id+"F0.wireOp",EDGE,"E14.1"),sQuery(id+"F0.wireOp",EDGE,"E14.2"),sQuery(id+"F0.wireOp",EDGE,"E14.3"),sQuery(id+"F0.wireOp",EDGE,"E14.4"),sQuery(id+"F0.wireOp",EDGE,"E14.5"),sQuery(id+"F0.wireOp",EDGE,"E15.1"),sQuery(id+"F0.wireOp",EDGE,"E15.2"),sQuery(id+"F0.wireOp",EDGE,"E15.3"),sQuery(id+"F0.wireOp",EDGE,"E15.4"),sQuery(id+"F0.wireOp",EDGE,"E15.5"),sQuery(id+"F0.wireOp",EDGE,"E19.1"),sQuery(id+"F0.wireOp",EDGE,"E19.2"),sQuery(id+"F0.wireOp",EDGE,"E19.3"),sQuery(id+"F0.wireOp",EDGE,"E19.4"),sQuery(id+"F0.wireOp",EDGE,"E19.5")])],"isStart":true});
            var sketch = newSketch(context, id + "F9", { "sketchPlane" : qUnion([Q0])});
            skLineSegment(sketch, "E20", {"start": v(29.44, -9) * mm, "end": v(18.48, -9) * mm});
            skLineSegment(sketch, "E21", {"start": v(18.48, -9) * mm, "end": v(17.03, -11.5) * mm});
            skLineSegment(sketch, "E22", {"start": v(17.03, -11.5) * mm, "end": v(22.52, -21) * mm});
            skLineSegment(sketch, "E23", {"start": v(22.52, -21) * mm, "end": v(36.37, -21) * mm});
            skLineSegment(sketch, "E24", {"start": v(36.37, -21) * mm, "end": v(29.44, -9) * mm});
            skLineSegment(sketch, "E25", {"start": v(-17.03, -11.5) * mm, "end": v(-22.52, -21) * mm});
            skLineSegment(sketch, "E26", {"start": v(-22.52, -21) * mm, "end": v(-36.37, -21) * mm});
            skLineSegment(sketch, "E27", {"start": v(-36.37, -21) * mm, "end": v(-29.44, -9) * mm});
            skLineSegment(sketch, "E28", {"start": v(-29.44, -9) * mm, "end": v(-18.48, -9) * mm});
            skLineSegment(sketch, "E29", {"start": v(-18.48, -9) * mm, "end": v(-17.03, -11.5) * mm});
            skLineSegment(sketch, "E30", {"start": v(1.44, 20.5) * mm, "end": v(-1.44, 20.5) * mm});
            skLineSegment(sketch, "E31", {"start": v(-1.44, 20.5) * mm, "end": v(-6.93, 30) * mm});
            skLineSegment(sketch, "E32", {"start": v(-6.93, 30) * mm, "end": v(0, 42) * mm});
            skLineSegment(sketch, "E33", {"start": v(0, 42) * mm, "end": v(6.93, 30) * mm});
            skLineSegment(sketch, "E34", {"start": v(6.93, 30) * mm, "end": v(1.44, 20.5) * mm});
            skSolve(sketch);
        }
        {
            var Q0;
            {var subQ0=sQuery(id+"F0.wireOp",EDGE,"E19.5");var subQ1=sQuery(id+"F0.wireOp",EDGE,"E19.4");var subQ2=sQuery(id+"F0.wireOp",EDGE,"E19.3");var subQ3=sQuery(id+"F0.wireOp",EDGE,"E19.2");var subQ4=sQuery(id+"F0.wireOp",EDGE,"E19.1");var subQ5=sQuery(id+"F0.wireOp",EDGE,"E15.5");var subQ6=sQuery(id+"F0.wireOp",EDGE,"E15.4");var subQ7=sQuery(id+"F0.wireOp",EDGE,"E15.3");var subQ8=sQuery(id+"F0.wireOp",EDGE,"E15.2");var subQ9=sQuery(id+"F0.wireOp",EDGE,"E15.1");var subQ10=sQuery(id+"F0.wireOp",EDGE,"E14.5");var subQ11=sQuery(id+"F0.wireOp",EDGE,"E14.4");var subQ12=sQuery(id+"F0.wireOp",EDGE,"E14.3");var subQ13=sQuery(id+"F0.wireOp",EDGE,"E14.2");var subQ14=sQuery(id+"F0.wireOp",EDGE,"E14.1");var subQ15=sQuery(id+"F0.wireOp",EDGE,"E2.4");var subQ16=sQuery(id+"F0.wireOp",EDGE,"E2.2");var subQ17=sQuery(id+"F0.wireOp",EDGE,"E2.0");var subQ18=sQuery(id+"F0.wireOp",EDGE,"E0");var subQ19=makeQuery(id+"F1.opExtrude","CAP_FACE",FACE,{"disambiguationData":[OSD([subQ18,subQ17,subQ16,subQ15,subQ14,subQ13,subQ12,subQ11,subQ10,subQ9,subQ8,subQ7,subQ6,subQ5,subQ4,subQ3,subQ2,subQ1,subQ0])],"isStart":true});Q0=makeQuery(id+"F8.opChamfer","BLEND_FACE",FACE,{"disambiguationData":[OSD([subQ18,subQ17,subQ16,subQ15,subQ14,subQ13,subQ12,subQ11,subQ10,subQ9,subQ8,subQ7,subQ6,subQ5,subQ4,subQ3,subQ2,subQ1,subQ0]),TDD([makeQuery(id+"F7.opChamfer","BLEND_EDGE",EDGE,{"blendedFrom":[makeQuery(id+"F2.opChamfer","BLEND_EDGE",EDGE,{"blendedFrom":[makeQuery(id+"F1.opExtrude","CAP_EDGE",EDGE,{"disambiguationData":[OSD([subQ13])],"isStart":true}),subQ19],"blendedInto":[subQ19]}),subQ19],"blendedInto":[subQ19]})])]});}
            var Q1;
            Q1=makeQuery(id+"F9.imprint","IMPRINT",FACE,{"disambiguationData":[TD([[makeQuery(id+"F9.imprint","IMPRINT",EDGE,{"derivedFrom":sQuery(id+"F9.wireOp",EDGE,"E20")}),1.0]])]});
            var Q2;
            {var subQ0=sQuery(id+"F0.wireOp",EDGE,"E19.5");var subQ1=sQuery(id+"F0.wireOp",EDGE,"E19.4");var subQ2=sQuery(id+"F0.wireOp",EDGE,"E19.3");var subQ3=sQuery(id+"F0.wireOp",EDGE,"E19.2");var subQ4=sQuery(id+"F0.wireOp",EDGE,"E19.1");var subQ5=sQuery(id+"F0.wireOp",EDGE,"E15.5");var subQ6=sQuery(id+"F0.wireOp",EDGE,"E15.4");var subQ7=sQuery(id+"F0.wireOp",EDGE,"E15.3");var subQ8=sQuery(id+"F0.wireOp",EDGE,"E15.2");var subQ9=sQuery(id+"F0.wireOp",EDGE,"E15.1");var subQ10=sQuery(id+"F0.wireOp",EDGE,"E14.5");var subQ11=sQuery(id+"F0.wireOp",EDGE,"E14.4");var subQ12=sQuery(id+"F0.wireOp",EDGE,"E14.3");var subQ13=sQuery(id+"F0.wireOp",EDGE,"E14.2");var subQ14=sQuery(id+"F0.wireOp",EDGE,"E14.1");var subQ15=sQuery(id+"F0.wireOp",EDGE,"E2.4");var subQ16=sQuery(id+"F0.wireOp",EDGE,"E2.2");var subQ17=sQuery(id+"F0.wireOp",EDGE,"E2.0");var subQ18=sQuery(id+"F0.wireOp",EDGE,"E0");var subQ19=makeQuery(id+"F1.opExtrude","CAP_FACE",FACE,{"disambiguationData":[OSD([subQ18,subQ17,subQ16,subQ15,subQ14,subQ13,subQ12,subQ11,subQ10,subQ9,subQ8,subQ7,subQ6,subQ5,subQ4,subQ3,subQ2,subQ1,subQ0])],"isStart":true});Q2=makeQuery(id+"F8.opChamfer","BLEND_FACE",FACE,{"disambiguationData":[OSD([subQ18,subQ17,subQ16,subQ15,subQ14,subQ13,subQ12,subQ11,subQ10,subQ9,subQ8,subQ7,subQ6,subQ5,subQ4,subQ3,subQ2,subQ1,subQ0]),TDD([makeQuery(id+"F7.opChamfer","BLEND_EDGE",EDGE,{"blendedFrom":[makeQuery(id+"F2.opChamfer","BLEND_EDGE",EDGE,{"blendedFrom":[makeQuery(id+"F1.opExtrude","CAP_EDGE",EDGE,{"disambiguationData":[OSD([subQ11])],"isStart":true}),subQ19],"blendedInto":[subQ19]}),subQ19],"blendedInto":[subQ19]})])]});}
            var Q3;
            {var subQ0=sQuery(id+"F0.wireOp",EDGE,"E19.5");var subQ1=sQuery(id+"F0.wireOp",EDGE,"E19.4");var subQ2=sQuery(id+"F0.wireOp",EDGE,"E19.3");var subQ3=sQuery(id+"F0.wireOp",EDGE,"E19.2");var subQ4=sQuery(id+"F0.wireOp",EDGE,"E19.1");var subQ5=sQuery(id+"F0.wireOp",EDGE,"E15.5");var subQ6=sQuery(id+"F0.wireOp",EDGE,"E15.4");var subQ7=sQuery(id+"F0.wireOp",EDGE,"E15.3");var subQ8=sQuery(id+"F0.wireOp",EDGE,"E15.2");var subQ9=sQuery(id+"F0.wireOp",EDGE,"E15.1");var subQ10=sQuery(id+"F0.wireOp",EDGE,"E14.5");var subQ11=sQuery(id+"F0.wireOp",EDGE,"E14.4");var subQ12=sQuery(id+"F0.wireOp",EDGE,"E14.3");var subQ13=sQuery(id+"F0.wireOp",EDGE,"E14.2");var subQ14=sQuery(id+"F0.wireOp",EDGE,"E14.1");var subQ15=sQuery(id+"F0.wireOp",EDGE,"E2.4");var subQ16=sQuery(id+"F0.wireOp",EDGE,"E2.2");var subQ17=sQuery(id+"F0.wireOp",EDGE,"E2.0");var subQ18=sQuery(id+"F0.wireOp",EDGE,"E0");var subQ19=makeQuery(id+"F1.opExtrude","CAP_FACE",FACE,{"disambiguationData":[OSD([subQ18,subQ17,subQ16,subQ15,subQ14,subQ13,subQ12,subQ11,subQ10,subQ9,subQ8,subQ7,subQ6,subQ5,subQ4,subQ3,subQ2,subQ1,subQ0])],"isStart":true});Q3=makeQuery(id+"F8.opChamfer","BLEND_FACE",FACE,{"disambiguationData":[OSD([subQ18,subQ17,subQ16,subQ15,subQ14,subQ13,subQ12,subQ11,subQ10,subQ9,subQ8,subQ7,subQ6,subQ5,subQ4,subQ3,subQ2,subQ1,subQ0]),TDD([makeQuery(id+"F7.opChamfer","BLEND_EDGE",EDGE,{"blendedFrom":[makeQuery(id+"F2.opChamfer","BLEND_EDGE",EDGE,{"blendedFrom":[makeQuery(id+"F1.opExtrude","CAP_EDGE",EDGE,{"disambiguationData":[OSD([subQ6])],"isStart":true}),subQ19],"blendedInto":[subQ19]}),subQ19],"blendedInto":[subQ19]})])]});}
            var Q4;
            Q4=makeQuery(id+"F9.imprint","IMPRINT",FACE,{"disambiguationData":[TD([[makeQuery(id+"F9.imprint","IMPRINT",EDGE,{"derivedFrom":sQuery(id+"F9.wireOp",EDGE,"E25")}),1.0]])]});
            var Q5;
            {var subQ0=sQuery(id+"F0.wireOp",EDGE,"E19.5");var subQ1=sQuery(id+"F0.wireOp",EDGE,"E19.4");var subQ2=sQuery(id+"F0.wireOp",EDGE,"E19.3");var subQ3=sQuery(id+"F0.wireOp",EDGE,"E19.2");var subQ4=sQuery(id+"F0.wireOp",EDGE,"E19.1");var subQ5=sQuery(id+"F0.wireOp",EDGE,"E15.5");var subQ6=sQuery(id+"F0.wireOp",EDGE,"E15.4");var subQ7=sQuery(id+"F0.wireOp",EDGE,"E15.3");var subQ8=sQuery(id+"F0.wireOp",EDGE,"E15.2");var subQ9=sQuery(id+"F0.wireOp",EDGE,"E15.1");var subQ10=sQuery(id+"F0.wireOp",EDGE,"E14.5");var subQ11=sQuery(id+"F0.wireOp",EDGE,"E14.4");var subQ12=sQuery(id+"F0.wireOp",EDGE,"E14.3");var subQ13=sQuery(id+"F0.wireOp",EDGE,"E14.2");var subQ14=sQuery(id+"F0.wireOp",EDGE,"E14.1");var subQ15=sQuery(id+"F0.wireOp",EDGE,"E2.4");var subQ16=sQuery(id+"F0.wireOp",EDGE,"E2.2");var subQ17=sQuery(id+"F0.wireOp",EDGE,"E2.0");var subQ18=sQuery(id+"F0.wireOp",EDGE,"E0");var subQ19=makeQuery(id+"F1.opExtrude","CAP_FACE",FACE,{"disambiguationData":[OSD([subQ18,subQ17,subQ16,subQ15,subQ14,subQ13,subQ12,subQ11,subQ10,subQ9,subQ8,subQ7,subQ6,subQ5,subQ4,subQ3,subQ2,subQ1,subQ0])],"isStart":true});Q5=makeQuery(id+"F8.opChamfer","BLEND_FACE",FACE,{"disambiguationData":[OSD([subQ18,subQ17,subQ16,subQ15,subQ14,subQ13,subQ12,subQ11,subQ10,subQ9,subQ8,subQ7,subQ6,subQ5,subQ4,subQ3,subQ2,subQ1,subQ0]),TDD([makeQuery(id+"F7.opChamfer","BLEND_EDGE",EDGE,{"blendedFrom":[makeQuery(id+"F2.opChamfer","BLEND_EDGE",EDGE,{"blendedFrom":[makeQuery(id+"F1.opExtrude","CAP_EDGE",EDGE,{"disambiguationData":[OSD([subQ8])],"isStart":true}),subQ19],"blendedInto":[subQ19]}),subQ19],"blendedInto":[subQ19]})])]});}
            var Q6;
            Q6=makeQuery(id+"F9.imprint","IMPRINT",FACE,{"disambiguationData":[TD([[makeQuery(id+"F9.imprint","IMPRINT",EDGE,{"derivedFrom":sQuery(id+"F9.wireOp",EDGE,"E30")}),-1.0]])]});
            var Q7;
            {var subQ0=sQuery(id+"F0.wireOp",EDGE,"E19.5");var subQ1=sQuery(id+"F0.wireOp",EDGE,"E19.4");var subQ2=sQuery(id+"F0.wireOp",EDGE,"E19.3");var subQ3=sQuery(id+"F0.wireOp",EDGE,"E19.2");var subQ4=sQuery(id+"F0.wireOp",EDGE,"E19.1");var subQ5=sQuery(id+"F0.wireOp",EDGE,"E15.5");var subQ6=sQuery(id+"F0.wireOp",EDGE,"E15.4");var subQ7=sQuery(id+"F0.wireOp",EDGE,"E15.3");var subQ8=sQuery(id+"F0.wireOp",EDGE,"E15.2");var subQ9=sQuery(id+"F0.wireOp",EDGE,"E15.1");var subQ10=sQuery(id+"F0.wireOp",EDGE,"E14.5");var subQ11=sQuery(id+"F0.wireOp",EDGE,"E14.4");var subQ12=sQuery(id+"F0.wireOp",EDGE,"E14.3");var subQ13=sQuery(id+"F0.wireOp",EDGE,"E14.2");var subQ14=sQuery(id+"F0.wireOp",EDGE,"E14.1");var subQ15=sQuery(id+"F0.wireOp",EDGE,"E2.4");var subQ16=sQuery(id+"F0.wireOp",EDGE,"E2.2");var subQ17=sQuery(id+"F0.wireOp",EDGE,"E2.0");var subQ18=sQuery(id+"F0.wireOp",EDGE,"E0");var subQ19=makeQuery(id+"F1.opExtrude","CAP_FACE",FACE,{"disambiguationData":[OSD([subQ18,subQ17,subQ16,subQ15,subQ14,subQ13,subQ12,subQ11,subQ10,subQ9,subQ8,subQ7,subQ6,subQ5,subQ4,subQ3,subQ2,subQ1,subQ0])],"isStart":true});Q7=makeQuery(id+"F8.opChamfer","BLEND_FACE",FACE,{"disambiguationData":[OSD([subQ18,subQ17,subQ16,subQ15,subQ14,subQ13,subQ12,subQ11,subQ10,subQ9,subQ8,subQ7,subQ6,subQ5,subQ4,subQ3,subQ2,subQ1,subQ0]),TDD([makeQuery(id+"F7.opChamfer","BLEND_EDGE",EDGE,{"blendedFrom":[makeQuery(id+"F2.opChamfer","BLEND_EDGE",EDGE,{"blendedFrom":[makeQuery(id+"F1.opExtrude","CAP_EDGE",EDGE,{"disambiguationData":[OSD([subQ1])],"isStart":true}),subQ19],"blendedInto":[subQ19]}),subQ19],"blendedInto":[subQ19]})])]});}
            var Q8;
            {var subQ0=sQuery(id+"F0.wireOp",EDGE,"E19.5");var subQ1=sQuery(id+"F0.wireOp",EDGE,"E19.4");var subQ2=sQuery(id+"F0.wireOp",EDGE,"E19.3");var subQ3=sQuery(id+"F0.wireOp",EDGE,"E19.2");var subQ4=sQuery(id+"F0.wireOp",EDGE,"E19.1");var subQ5=sQuery(id+"F0.wireOp",EDGE,"E15.5");var subQ6=sQuery(id+"F0.wireOp",EDGE,"E15.4");var subQ7=sQuery(id+"F0.wireOp",EDGE,"E15.3");var subQ8=sQuery(id+"F0.wireOp",EDGE,"E15.2");var subQ9=sQuery(id+"F0.wireOp",EDGE,"E15.1");var subQ10=sQuery(id+"F0.wireOp",EDGE,"E14.5");var subQ11=sQuery(id+"F0.wireOp",EDGE,"E14.4");var subQ12=sQuery(id+"F0.wireOp",EDGE,"E14.3");var subQ13=sQuery(id+"F0.wireOp",EDGE,"E14.2");var subQ14=sQuery(id+"F0.wireOp",EDGE,"E14.1");var subQ15=sQuery(id+"F0.wireOp",EDGE,"E2.4");var subQ16=sQuery(id+"F0.wireOp",EDGE,"E2.2");var subQ17=sQuery(id+"F0.wireOp",EDGE,"E2.0");var subQ18=sQuery(id+"F0.wireOp",EDGE,"E0");var subQ19=makeQuery(id+"F1.opExtrude","CAP_FACE",FACE,{"disambiguationData":[OSD([subQ18,subQ17,subQ16,subQ15,subQ14,subQ13,subQ12,subQ11,subQ10,subQ9,subQ8,subQ7,subQ6,subQ5,subQ4,subQ3,subQ2,subQ1,subQ0])],"isStart":true});Q8=makeQuery(id+"F8.opChamfer","BLEND_FACE",FACE,{"disambiguationData":[OSD([subQ18,subQ17,subQ16,subQ15,subQ14,subQ13,subQ12,subQ11,subQ10,subQ9,subQ8,subQ7,subQ6,subQ5,subQ4,subQ3,subQ2,subQ1,subQ0]),TDD([makeQuery(id+"F7.opChamfer","BLEND_EDGE",EDGE,{"blendedFrom":[makeQuery(id+"F2.opChamfer","BLEND_EDGE",EDGE,{"blendedFrom":[makeQuery(id+"F1.opExtrude","CAP_EDGE",EDGE,{"disambiguationData":[OSD([subQ3])],"isStart":true}),subQ19],"blendedInto":[subQ19]}),subQ19],"blendedInto":[subQ19]})])]});}
            var Q9;
            Q9=makeQuery(id+"F1.opExtrude","SWEPT_FACE",FACE,{"disambiguationData":[OSD([sQuery(id+"F0.wireOp",EDGE,"E14.3")])]});
            var Q10;
            Q10=makeQuery(id+"F1.opExtrude","SWEPT_FACE",FACE,{"disambiguationData":[OSD([sQuery(id+"F0.wireOp",EDGE,"E15.3")])]});
            var Q11;
            Q11=makeQuery(id+"F1.opExtrude","SWEPT_FACE",FACE,{"disambiguationData":[OSD([sQuery(id+"F0.wireOp",EDGE,"E19.3")])]});
            extrude(context, id + "F10", {"entities" : qUnion([Q0, Q1, Q2, Q3, Q4, Q5, Q6, Q7, Q8, Q9, Q10, Q11]), "operationType" : NewBodyOperationType.REMOVE, "oppositeDirection" : true, "depth" : 25 * mm, "offsetDistance" : 25 * mm});
        }
    });
